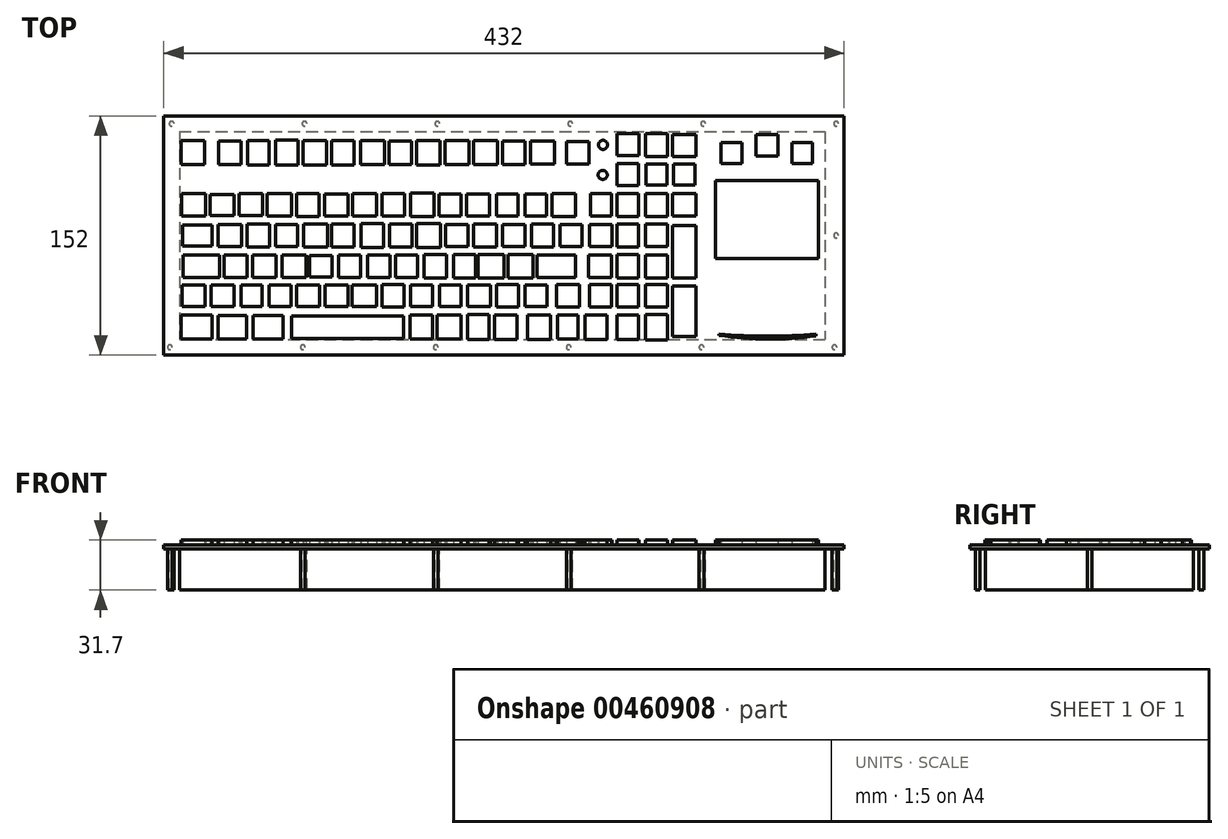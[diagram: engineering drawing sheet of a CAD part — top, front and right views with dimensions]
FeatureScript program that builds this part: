
annotation { "Feature Type Name" : "Feature", "Feature Type Description" : "" }
export const myFeature = defineFeature(function(context is Context, id is Id, definition is map)
    precondition{}
    {
        {
            var Q0;
            Q0=qCreatedBy(makeId("Top.planeOp"),FACE);
            var sketch = newSketch(context, id + "F0", { "sketchPlane" : qUnion([Q0])});
            skLineSegment(sketch, "E0.bottom", {"start": v(216, 76) * mm, "end": v(-216, 76) * mm});
            skLineSegment(sketch, "E0.top", {"start": v(216, -76) * mm, "end": v(-216, -76) * mm});
            skLineSegment(sketch, "E0.left", {"start": v(216, 76) * mm, "end": v(216, -76) * mm});
            skLineSegment(sketch, "E0.right", {"start": v(-216, 76) * mm, "end": v(-216, -76) * mm});
            skPoint(sketch, "E0.middle", {"position": v(0, 0) * mm});
            skLineSegment(sketch, "E1", {"start": v(-197.56, 52.6) * mm, "end": v(47, 52.6) * mm, "construction": true});
            skLineSegment(sketch, "E2", {"start": v(78.75, 57.78) * mm, "end": v(78.75, -58.22) * mm, "construction": true});
            skLineSegment(sketch, "E3", {"start": v(96.86, 57.48) * mm, "end": v(96.86, -58.22) * mm, "construction": true});
            skLineSegment(sketch, "E4", {"start": v(114.66, 58.09) * mm, "end": v(114.66, -58.22) * mm, "construction": true});
            skLineSegment(sketch, "E5", {"start": v(-195.3, -58.22) * mm, "end": v(114.66, -58.22) * mm, "construction": true});
            skLineSegment(sketch, "E6", {"start": v(-197.14, -38.27) * mm, "end": v(114.66, -38.27) * mm, "construction": true});
            skLineSegment(sketch, "E7", {"start": v(-196.22, -19.55) * mm, "end": v(114.66, -19.55) * mm, "construction": true});
            skLineSegment(sketch, "E8", {"start": v(-194.68, 0) * mm, "end": v(114.66, 0) * mm, "construction": true});
            skLineSegment(sketch, "E9", {"start": v(-197.14, 19.42) * mm, "end": v(114.66, 19.42) * mm, "construction": true});
            skLineSegment(sketch, "E10", {"start": v(134.3, -14.64) * mm, "end": v(199.67, 34.77) * mm, "construction": true});
            skLineSegment(sketch, "E11", {"start": v(137.98, 45.81) * mm, "end": v(151.36, 59.04) * mm, "construction": true});
            skLineSegment(sketch, "E12", {"start": v(160.21, 50.47) * mm, "end": v(174.17, 64.15) * mm, "construction": true});
            skLineSegment(sketch, "E13", {"start": v(183.02, 45.63) * mm, "end": v(196.16, 58.95) * mm, "construction": true});
            skLineSegment(sketch, "E14", {"start": v(78.75, 38.8) * mm, "end": v(114.66, 38.8) * mm, "construction": true});
            skLineSegment(sketch, "E15.bottom", {"start": v(199.67, 34.77) * mm, "end": v(134.3, 34.77) * mm});
            skLineSegment(sketch, "E15.top", {"start": v(199.67, -14.64) * mm, "end": v(134.3, -14.64) * mm});
            skLineSegment(sketch, "E15.left", {"start": v(199.67, 34.77) * mm, "end": v(199.67, -14.64) * mm});
            skLineSegment(sketch, "E15.right", {"start": v(134.3, 34.77) * mm, "end": v(134.3, -14.64) * mm});
            skPoint(sketch, "E15.middle", {"position": v(166.98, 10.06) * mm});
            skLineSegment(sketch, "E16.bottom", {"start": v(151.36, 59.04) * mm, "end": v(137.98, 59.04) * mm});
            skLineSegment(sketch, "E16.top", {"start": v(151.36, 45.81) * mm, "end": v(137.98, 45.81) * mm});
            skLineSegment(sketch, "E16.left", {"start": v(151.36, 59.04) * mm, "end": v(151.36, 45.81) * mm});
            skLineSegment(sketch, "E16.right", {"start": v(137.98, 59.04) * mm, "end": v(137.98, 45.81) * mm});
            skPoint(sketch, "E16.middle", {"position": v(144.67, 52.43) * mm});
            skLineSegment(sketch, "E17.bottom", {"start": v(174.17, 64.15) * mm, "end": v(160.21, 64.15) * mm});
            skLineSegment(sketch, "E17.top", {"start": v(174.17, 50.47) * mm, "end": v(160.21, 50.47) * mm});
            skLineSegment(sketch, "E17.left", {"start": v(174.17, 64.15) * mm, "end": v(174.17, 50.47) * mm});
            skLineSegment(sketch, "E17.right", {"start": v(160.21, 64.15) * mm, "end": v(160.21, 50.47) * mm});
            skPoint(sketch, "E17.middle", {"position": v(167.2, 57.31) * mm});
            skLineSegment(sketch, "E18.bottom", {"start": v(196.16, 58.95) * mm, "end": v(183.02, 58.95) * mm});
            skLineSegment(sketch, "E18.top", {"start": v(196.16, 45.63) * mm, "end": v(183.02, 45.63) * mm});
            skLineSegment(sketch, "E18.left", {"start": v(196.16, 58.95) * mm, "end": v(196.16, 45.63) * mm});
            skLineSegment(sketch, "E18.right", {"start": v(183.02, 58.95) * mm, "end": v(183.02, 45.63) * mm});
            skPoint(sketch, "E18.middle", {"position": v(189.59, 52.3) * mm});
            skLineSegment(sketch, "E19.bottom", {"start": v(122.07, 64.09) * mm, "end": v(107.24, 64.09) * mm});
            skLineSegment(sketch, "E19.top", {"start": v(122.07, 50.04) * mm, "end": v(107.24, 50.04) * mm});
            skLineSegment(sketch, "E19.left", {"start": v(122.07, 64.09) * mm, "end": v(122.07, 50.04) * mm});
            skLineSegment(sketch, "E19.right", {"start": v(107.24, 64.09) * mm, "end": v(107.24, 50.04) * mm});
            skPoint(sketch, "E19.middle", {"position": v(114.66, 57.06) * mm});
            skLineSegment(sketch, "E20.bottom", {"start": v(103.83, 64.73) * mm, "end": v(89.9, 64.73) * mm});
            skLineSegment(sketch, "E20.top", {"start": v(103.83, 50.22) * mm, "end": v(89.9, 50.22) * mm});
            skLineSegment(sketch, "E20.left", {"start": v(103.83, 64.73) * mm, "end": v(103.83, 50.22) * mm});
            skLineSegment(sketch, "E20.right", {"start": v(89.9, 64.73) * mm, "end": v(89.9, 50.22) * mm});
            skPoint(sketch, "E20.middle", {"position": v(96.86, 57.48) * mm});
            skLineSegment(sketch, "E21.bottom", {"start": v(85.76, 64.73) * mm, "end": v(71.75, 64.73) * mm});
            skLineSegment(sketch, "E21.top", {"start": v(85.76, 50.84) * mm, "end": v(71.75, 50.84) * mm});
            skLineSegment(sketch, "E21.left", {"start": v(85.76, 64.73) * mm, "end": v(85.76, 50.84) * mm});
            skLineSegment(sketch, "E21.right", {"start": v(71.75, 64.73) * mm, "end": v(71.75, 50.84) * mm});
            skPoint(sketch, "E21.middle", {"position": v(78.75, 57.78) * mm});
            skLineSegment(sketch, "E22.bottom", {"start": v(85.67, 45.75) * mm, "end": v(71.84, 45.75) * mm});
            skLineSegment(sketch, "E22.top", {"start": v(85.67, 31.84) * mm, "end": v(71.84, 31.84) * mm});
            skLineSegment(sketch, "E22.left", {"start": v(85.67, 45.75) * mm, "end": v(85.67, 31.84) * mm});
            skLineSegment(sketch, "E22.right", {"start": v(71.84, 45.75) * mm, "end": v(71.84, 31.84) * mm});
            skPoint(sketch, "E22.middle", {"position": v(78.75, 38.8) * mm});
            skLineSegment(sketch, "E23.bottom", {"start": v(103.55, 45.48) * mm, "end": v(90.17, 45.48) * mm});
            skLineSegment(sketch, "E23.top", {"start": v(103.55, 32.1) * mm, "end": v(90.17, 32.1) * mm});
            skLineSegment(sketch, "E23.left", {"start": v(103.55, 45.48) * mm, "end": v(103.55, 32.1) * mm});
            skLineSegment(sketch, "E23.right", {"start": v(90.17, 45.48) * mm, "end": v(90.17, 32.1) * mm});
            skPoint(sketch, "E23.middle", {"position": v(96.86, 38.8) * mm});
            skLineSegment(sketch, "E24.bottom", {"start": v(121.53, 45.39) * mm, "end": v(107.8, 45.39) * mm});
            skLineSegment(sketch, "E24.top", {"start": v(121.53, 32.2) * mm, "end": v(107.8, 32.2) * mm});
            skLineSegment(sketch, "E24.left", {"start": v(121.53, 45.39) * mm, "end": v(121.53, 32.2) * mm});
            skLineSegment(sketch, "E24.right", {"start": v(107.8, 45.39) * mm, "end": v(107.8, 32.2) * mm});
            skPoint(sketch, "E24.middle", {"position": v(114.66, 38.8) * mm});
            skLineSegment(sketch, "E25.bottom", {"start": v(122.07, 26.58) * mm, "end": v(107.24, 26.58) * mm});
            skLineSegment(sketch, "E25.top", {"start": v(122.07, 12.26) * mm, "end": v(107.24, 12.26) * mm});
            skLineSegment(sketch, "E25.left", {"start": v(122.07, 26.58) * mm, "end": v(122.07, 12.26) * mm});
            skLineSegment(sketch, "E25.right", {"start": v(107.24, 26.58) * mm, "end": v(107.24, 12.26) * mm});
            skPoint(sketch, "E25.middle", {"position": v(114.66, 19.42) * mm});
            skLineSegment(sketch, "E26.bottom", {"start": v(103.86, 26.67) * mm, "end": v(89.86, 26.67) * mm});
            skLineSegment(sketch, "E26.top", {"start": v(103.86, 12.17) * mm, "end": v(89.86, 12.17) * mm});
            skLineSegment(sketch, "E26.left", {"start": v(103.86, 26.67) * mm, "end": v(103.86, 12.17) * mm});
            skLineSegment(sketch, "E26.right", {"start": v(89.86, 26.67) * mm, "end": v(89.86, 12.17) * mm});
            skPoint(sketch, "E26.middle", {"position": v(96.86, 19.42) * mm});
            skLineSegment(sketch, "E27.bottom", {"start": v(85.61, 26.76) * mm, "end": v(71.9, 26.76) * mm});
            skLineSegment(sketch, "E27.top", {"start": v(85.61, 12.08) * mm, "end": v(71.9, 12.08) * mm});
            skLineSegment(sketch, "E27.left", {"start": v(85.61, 26.76) * mm, "end": v(85.61, 12.08) * mm});
            skLineSegment(sketch, "E27.right", {"start": v(71.9, 26.76) * mm, "end": v(71.9, 12.08) * mm});
            skPoint(sketch, "E27.middle", {"position": v(78.75, 19.42) * mm});
            skLineSegment(sketch, "E28.bottom", {"start": v(122.07, 6.26) * mm, "end": v(107.24, 6.26) * mm});
            skLineSegment(sketch, "E28.top", {"start": v(122.07, -27.15) * mm, "end": v(107.24, -27.15) * mm});
            skLineSegment(sketch, "E28.left", {"start": v(122.07, 6.26) * mm, "end": v(122.07, -27.15) * mm});
            skLineSegment(sketch, "E28.right", {"start": v(107.24, 6.26) * mm, "end": v(107.24, -27.15) * mm});
            skPoint(sketch, "E28.middle", {"position": v(114.66, -10.45) * mm});
            skLineSegment(sketch, "E29.bottom", {"start": v(122.07, -31.95) * mm, "end": v(107.24, -31.95) * mm});
            skLineSegment(sketch, "E29.top", {"start": v(122.07, -64.28) * mm, "end": v(107.24, -64.28) * mm});
            skLineSegment(sketch, "E29.left", {"start": v(122.07, -31.95) * mm, "end": v(122.07, -64.28) * mm});
            skLineSegment(sketch, "E29.right", {"start": v(107.24, -31.95) * mm, "end": v(107.24, -64.28) * mm});
            skPoint(sketch, "E29.middle", {"position": v(114.66, -48.11) * mm});
            skLineSegment(sketch, "E30.bottom", {"start": v(103.79, 7.16) * mm, "end": v(89.93, 7.16) * mm});
            skLineSegment(sketch, "E30.top", {"start": v(103.79, -7.16) * mm, "end": v(89.93, -7.16) * mm});
            skLineSegment(sketch, "E30.left", {"start": v(103.79, 7.16) * mm, "end": v(103.79, -7.16) * mm});
            skLineSegment(sketch, "E30.right", {"start": v(89.93, 7.16) * mm, "end": v(89.93, -7.16) * mm});
            skPoint(sketch, "E30.middle", {"position": v(96.86, 0) * mm});
            skLineSegment(sketch, "E31.bottom", {"start": v(85.61, 7.39) * mm, "end": v(71.9, 7.39) * mm});
            skLineSegment(sketch, "E31.top", {"start": v(85.61, -7.39) * mm, "end": v(71.9, -7.39) * mm});
            skLineSegment(sketch, "E31.left", {"start": v(85.61, 7.39) * mm, "end": v(85.61, -7.39) * mm});
            skLineSegment(sketch, "E31.right", {"start": v(71.9, 7.39) * mm, "end": v(71.9, -7.39) * mm});
            skPoint(sketch, "E31.middle", {"position": v(78.75, 0) * mm});
            skLineSegment(sketch, "E32.bottom", {"start": v(85.61, -12.18) * mm, "end": v(71.9, -12.18) * mm});
            skLineSegment(sketch, "E32.top", {"start": v(85.61, -26.93) * mm, "end": v(71.9, -26.93) * mm});
            skLineSegment(sketch, "E32.left", {"start": v(85.61, -12.18) * mm, "end": v(85.61, -26.93) * mm});
            skLineSegment(sketch, "E32.right", {"start": v(71.9, -12.18) * mm, "end": v(71.9, -26.93) * mm});
            skPoint(sketch, "E32.middle", {"position": v(78.75, -19.55) * mm});
            skLineSegment(sketch, "E33.bottom", {"start": v(103.86, -12.25) * mm, "end": v(89.86, -12.25) * mm});
            skLineSegment(sketch, "E33.top", {"start": v(103.86, -26.85) * mm, "end": v(89.86, -26.85) * mm});
            skLineSegment(sketch, "E33.left", {"start": v(103.86, -12.25) * mm, "end": v(103.86, -26.85) * mm});
            skLineSegment(sketch, "E33.right", {"start": v(89.86, -12.25) * mm, "end": v(89.86, -26.85) * mm});
            skPoint(sketch, "E33.middle", {"position": v(96.86, -19.55) * mm});
            skLineSegment(sketch, "E34.bottom", {"start": v(85.61, -31.27) * mm, "end": v(71.9, -31.27) * mm});
            skLineSegment(sketch, "E34.top", {"start": v(85.61, -45.28) * mm, "end": v(71.9, -45.28) * mm});
            skLineSegment(sketch, "E34.left", {"start": v(85.61, -31.27) * mm, "end": v(85.61, -45.28) * mm});
            skLineSegment(sketch, "E34.right", {"start": v(71.9, -31.27) * mm, "end": v(71.9, -45.28) * mm});
            skPoint(sketch, "E34.middle", {"position": v(78.75, -38.27) * mm});
            skLineSegment(sketch, "E35.bottom", {"start": v(103.86, -31.18) * mm, "end": v(89.86, -31.18) * mm});
            skLineSegment(sketch, "E35.top", {"start": v(103.86, -45.37) * mm, "end": v(89.86, -45.37) * mm});
            skLineSegment(sketch, "E35.left", {"start": v(103.86, -31.18) * mm, "end": v(103.86, -45.37) * mm});
            skLineSegment(sketch, "E35.right", {"start": v(89.86, -31.18) * mm, "end": v(89.86, -45.37) * mm});
            skPoint(sketch, "E35.middle", {"position": v(96.86, -38.27) * mm});
            skLineSegment(sketch, "E36.bottom", {"start": v(85.61, -50.52) * mm, "end": v(71.9, -50.52) * mm});
            skLineSegment(sketch, "E36.top", {"start": v(85.61, -65.92) * mm, "end": v(71.9, -65.92) * mm});
            skLineSegment(sketch, "E36.left", {"start": v(85.61, -50.52) * mm, "end": v(85.61, -65.92) * mm});
            skLineSegment(sketch, "E36.right", {"start": v(71.9, -50.52) * mm, "end": v(71.9, -65.92) * mm});
            skPoint(sketch, "E36.middle", {"position": v(78.75, -58.22) * mm});
            skLineSegment(sketch, "E37.bottom", {"start": v(103.86, -50.15) * mm, "end": v(89.86, -50.15) * mm});
            skLineSegment(sketch, "E37.top", {"start": v(103.86, -66.28) * mm, "end": v(89.86, -66.28) * mm});
            skLineSegment(sketch, "E37.left", {"start": v(103.86, -50.15) * mm, "end": v(103.86, -66.28) * mm});
            skLineSegment(sketch, "E37.right", {"start": v(89.86, -50.15) * mm, "end": v(89.86, -66.28) * mm});
            skPoint(sketch, "E37.middle", {"position": v(96.86, -58.22) * mm});
            skLineSegment(sketch, "E38.bottom", {"start": v(65.58, -50.52) * mm, "end": v(51.47, -50.52) * mm});
            skLineSegment(sketch, "E38.top", {"start": v(65.58, -65.92) * mm, "end": v(51.47, -65.92) * mm});
            skLineSegment(sketch, "E38.left", {"start": v(65.58, -50.52) * mm, "end": v(65.58, -65.92) * mm});
            skLineSegment(sketch, "E38.right", {"start": v(51.47, -50.52) * mm, "end": v(51.47, -65.92) * mm});
            skPoint(sketch, "E38.middle", {"position": v(58.53, -58.22) * mm});
            skPoint(sketch, "E38.cornerSnap0", {"position": v(78.75, -50.52) * mm});
            skLineSegment(sketch, "E39.bottom", {"start": v(47.24, -50.62) * mm, "end": v(34, -50.62) * mm});
            skLineSegment(sketch, "E39.top", {"start": v(47.24, -65.82) * mm, "end": v(34, -65.82) * mm});
            skLineSegment(sketch, "E39.left", {"start": v(47.24, -50.62) * mm, "end": v(47.24, -65.82) * mm});
            skLineSegment(sketch, "E39.right", {"start": v(34, -50.62) * mm, "end": v(34, -65.82) * mm});
            skPoint(sketch, "E39.middle", {"position": v(40.62, -58.22) * mm});
            skLineSegment(sketch, "E40.bottom", {"start": v(29.56, -50.4) * mm, "end": v(15.02, -50.4) * mm});
            skLineSegment(sketch, "E40.top", {"start": v(29.56, -66.04) * mm, "end": v(15.02, -66.04) * mm});
            skLineSegment(sketch, "E40.left", {"start": v(29.56, -50.4) * mm, "end": v(29.56, -66.04) * mm});
            skLineSegment(sketch, "E40.right", {"start": v(15.02, -50.4) * mm, "end": v(15.02, -66.04) * mm});
            skPoint(sketch, "E40.middle", {"position": v(22.29, -58.22) * mm});
            skLineSegment(sketch, "E41.bottom", {"start": v(8.4, -50.4) * mm, "end": v(-5.92, -50.4) * mm});
            skLineSegment(sketch, "E41.top", {"start": v(8.4, -66.04) * mm, "end": v(-5.92, -66.04) * mm});
            skLineSegment(sketch, "E41.left", {"start": v(8.4, -50.4) * mm, "end": v(8.4, -66.04) * mm});
            skLineSegment(sketch, "E41.right", {"start": v(-5.92, -50.4) * mm, "end": v(-5.92, -66.04) * mm});
            skPoint(sketch, "E41.middle", {"position": v(1.24, -58.22) * mm});
            skLineSegment(sketch, "E42.bottom", {"start": v(-9.28, -50.28) * mm, "end": v(-22.96, -50.28) * mm});
            skLineSegment(sketch, "E42.top", {"start": v(-9.28, -66.16) * mm, "end": v(-22.96, -66.16) * mm});
            skLineSegment(sketch, "E42.left", {"start": v(-9.28, -50.28) * mm, "end": v(-9.28, -66.16) * mm});
            skLineSegment(sketch, "E42.right", {"start": v(-22.96, -50.28) * mm, "end": v(-22.96, -66.16) * mm});
            skPoint(sketch, "E42.middle", {"position": v(-16.12, -58.22) * mm});
            skLineSegment(sketch, "E43.bottom", {"start": v(-27.34, -50.56) * mm, "end": v(-42.3, -50.56) * mm});
            skLineSegment(sketch, "E43.top", {"start": v(-27.34, -65.88) * mm, "end": v(-42.3, -65.88) * mm});
            skLineSegment(sketch, "E43.left", {"start": v(-27.34, -50.56) * mm, "end": v(-27.34, -65.88) * mm});
            skLineSegment(sketch, "E43.right", {"start": v(-42.3, -50.56) * mm, "end": v(-42.3, -65.88) * mm});
            skPoint(sketch, "E43.middle", {"position": v(-34.82, -58.22) * mm});
            skLineSegment(sketch, "E44.bottom", {"start": v(-45.4, -50.65) * mm, "end": v(-59.64, -50.65) * mm});
            skLineSegment(sketch, "E44.top", {"start": v(-45.4, -65.8) * mm, "end": v(-59.64, -65.8) * mm});
            skLineSegment(sketch, "E44.left", {"start": v(-45.4, -50.65) * mm, "end": v(-45.4, -65.8) * mm});
            skLineSegment(sketch, "E44.right", {"start": v(-59.64, -50.65) * mm, "end": v(-59.64, -65.8) * mm});
            skPoint(sketch, "E44.middle", {"position": v(-52.52, -58.22) * mm});
            skLineSegment(sketch, "E45.bottom", {"start": v(-63.58, -51.12) * mm, "end": v(-134.75, -51.12) * mm});
            skLineSegment(sketch, "E45.top", {"start": v(-63.58, -65.32) * mm, "end": v(-134.75, -65.32) * mm});
            skLineSegment(sketch, "E45.left", {"start": v(-63.58, -51.12) * mm, "end": v(-63.58, -65.32) * mm});
            skLineSegment(sketch, "E45.right", {"start": v(-134.75, -51.12) * mm, "end": v(-134.75, -65.32) * mm});
            skPoint(sketch, "E45.middle", {"position": v(-99.17, -58.22) * mm});
            skLineSegment(sketch, "E46.bottom", {"start": v(-140.19, -50.78) * mm, "end": v(-159.28, -50.78) * mm});
            skLineSegment(sketch, "E46.top", {"start": v(-140.19, -65.66) * mm, "end": v(-159.28, -65.66) * mm});
            skLineSegment(sketch, "E46.left", {"start": v(-140.19, -50.78) * mm, "end": v(-140.19, -65.66) * mm});
            skLineSegment(sketch, "E46.right", {"start": v(-159.28, -50.78) * mm, "end": v(-159.28, -65.66) * mm});
            skPoint(sketch, "E46.middle", {"position": v(-149.73, -58.22) * mm});
            skLineSegment(sketch, "E47.bottom", {"start": v(-163.28, -50.78) * mm, "end": v(-181.35, -50.78) * mm});
            skLineSegment(sketch, "E47.top", {"start": v(-163.28, -65.66) * mm, "end": v(-181.35, -65.66) * mm});
            skLineSegment(sketch, "E47.left", {"start": v(-163.28, -50.78) * mm, "end": v(-163.28, -65.66) * mm});
            skLineSegment(sketch, "E47.right", {"start": v(-181.35, -50.78) * mm, "end": v(-181.35, -65.66) * mm});
            skPoint(sketch, "E47.middle", {"position": v(-172.32, -58.22) * mm});
            skLineSegment(sketch, "E48.bottom", {"start": v(-185.45, -50.55) * mm, "end": v(-205.14, -50.55) * mm});
            skLineSegment(sketch, "E48.top", {"start": v(-185.45, -65.9) * mm, "end": v(-205.14, -65.9) * mm});
            skLineSegment(sketch, "E48.left", {"start": v(-185.45, -50.55) * mm, "end": v(-185.45, -65.9) * mm});
            skLineSegment(sketch, "E48.right", {"start": v(-205.14, -50.55) * mm, "end": v(-205.14, -65.9) * mm});
            skPoint(sketch, "E48.middle", {"position": v(-195.3, -58.22) * mm});
            skLineSegment(sketch, "E49.bottom", {"start": v(-189.83, -31.56) * mm, "end": v(-204.44, -31.56) * mm});
            skLineSegment(sketch, "E49.top", {"start": v(-189.83, -44.98) * mm, "end": v(-204.44, -44.98) * mm});
            skLineSegment(sketch, "E49.left", {"start": v(-189.83, -31.56) * mm, "end": v(-189.83, -44.98) * mm});
            skLineSegment(sketch, "E49.right", {"start": v(-204.44, -31.56) * mm, "end": v(-204.44, -44.98) * mm});
            skPoint(sketch, "E49.middle", {"position": v(-197.14, -38.27) * mm});
            skLineSegment(sketch, "E50.bottom", {"start": v(-171.39, -31.35) * mm, "end": v(-185.93, -31.35) * mm});
            skLineSegment(sketch, "E50.top", {"start": v(-171.39, -45.2) * mm, "end": v(-185.93, -45.2) * mm});
            skLineSegment(sketch, "E50.left", {"start": v(-171.39, -31.35) * mm, "end": v(-171.39, -45.2) * mm});
            skLineSegment(sketch, "E50.right", {"start": v(-185.93, -31.35) * mm, "end": v(-185.93, -45.2) * mm});
            skPoint(sketch, "E50.middle", {"position": v(-178.66, -38.27) * mm});
            skLineSegment(sketch, "E51.bottom", {"start": v(-153.48, -31.46) * mm, "end": v(-166.94, -31.46) * mm});
            skLineSegment(sketch, "E51.top", {"start": v(-153.48, -45.09) * mm, "end": v(-166.94, -45.09) * mm});
            skLineSegment(sketch, "E51.left", {"start": v(-153.48, -31.46) * mm, "end": v(-153.48, -45.09) * mm});
            skLineSegment(sketch, "E51.right", {"start": v(-166.94, -31.46) * mm, "end": v(-166.94, -45.09) * mm});
            skPoint(sketch, "E51.middle", {"position": v(-160.21, -38.27) * mm});
            skLineSegment(sketch, "E52.bottom", {"start": v(-135.26, -31.46) * mm, "end": v(-149.14, -31.46) * mm});
            skLineSegment(sketch, "E52.top", {"start": v(-135.26, -45.09) * mm, "end": v(-149.14, -45.09) * mm});
            skLineSegment(sketch, "E52.left", {"start": v(-135.26, -31.46) * mm, "end": v(-135.26, -45.09) * mm});
            skLineSegment(sketch, "E52.right", {"start": v(-149.14, -31.46) * mm, "end": v(-149.14, -45.09) * mm});
            skPoint(sketch, "E52.middle", {"position": v(-142.2, -38.27) * mm});
            skLineSegment(sketch, "E53.bottom", {"start": v(-117.03, -31.46) * mm, "end": v(-131.57, -31.46) * mm});
            skLineSegment(sketch, "E53.top", {"start": v(-117.03, -45.09) * mm, "end": v(-131.57, -45.09) * mm});
            skLineSegment(sketch, "E53.left", {"start": v(-117.03, -31.46) * mm, "end": v(-117.03, -45.09) * mm});
            skLineSegment(sketch, "E53.right", {"start": v(-131.57, -31.46) * mm, "end": v(-131.57, -45.09) * mm});
            skPoint(sketch, "E53.middle", {"position": v(-124.3, -38.27) * mm});
            skLineSegment(sketch, "E54.bottom", {"start": v(-98.9, -31.35) * mm, "end": v(-113.67, -31.35) * mm});
            skLineSegment(sketch, "E54.top", {"start": v(-98.9, -45.2) * mm, "end": v(-113.67, -45.2) * mm});
            skLineSegment(sketch, "E54.left", {"start": v(-98.9, -31.35) * mm, "end": v(-98.9, -45.2) * mm});
            skLineSegment(sketch, "E54.right", {"start": v(-113.67, -31.35) * mm, "end": v(-113.67, -45.2) * mm});
            skPoint(sketch, "E54.middle", {"position": v(-106.29, -38.27) * mm});
            skLineSegment(sketch, "E55.bottom", {"start": v(-80.86, -31.36) * mm, "end": v(-96.51, -31.36) * mm});
            skLineSegment(sketch, "E55.top", {"start": v(-80.86, -45.19) * mm, "end": v(-96.51, -45.19) * mm});
            skLineSegment(sketch, "E55.left", {"start": v(-80.86, -31.36) * mm, "end": v(-80.86, -45.19) * mm});
            skLineSegment(sketch, "E55.right", {"start": v(-96.51, -31.36) * mm, "end": v(-96.51, -45.19) * mm});
            skPoint(sketch, "E55.middle", {"position": v(-88.69, -38.27) * mm});
            skLineSegment(sketch, "E56.bottom", {"start": v(-63.52, -31.05) * mm, "end": v(-77.33, -31.05) * mm});
            skLineSegment(sketch, "E56.top", {"start": v(-63.52, -45.5) * mm, "end": v(-77.33, -45.5) * mm});
            skLineSegment(sketch, "E56.left", {"start": v(-63.52, -31.05) * mm, "end": v(-63.52, -45.5) * mm});
            skLineSegment(sketch, "E56.right", {"start": v(-77.33, -31.05) * mm, "end": v(-77.33, -45.5) * mm});
            skPoint(sketch, "E56.middle", {"position": v(-70.43, -38.27) * mm});
            skLineSegment(sketch, "E57.bottom", {"start": v(-45.4, -31.36) * mm, "end": v(-59.24, -31.36) * mm});
            skLineSegment(sketch, "E57.top", {"start": v(-45.4, -45.19) * mm, "end": v(-59.24, -45.19) * mm});
            skLineSegment(sketch, "E57.left", {"start": v(-45.4, -31.36) * mm, "end": v(-45.4, -45.19) * mm});
            skLineSegment(sketch, "E57.right", {"start": v(-59.24, -31.36) * mm, "end": v(-59.24, -45.19) * mm});
            skPoint(sketch, "E57.middle", {"position": v(-52.32, -38.27) * mm});
            skLineSegment(sketch, "E58.bottom", {"start": v(-27.31, -31.51) * mm, "end": v(-40.81, -31.51) * mm});
            skLineSegment(sketch, "E58.top", {"start": v(-27.31, -45.03) * mm, "end": v(-40.81, -45.03) * mm});
            skLineSegment(sketch, "E58.left", {"start": v(-27.31, -31.51) * mm, "end": v(-27.31, -45.03) * mm});
            skLineSegment(sketch, "E58.right", {"start": v(-40.81, -31.51) * mm, "end": v(-40.81, -45.03) * mm});
            skPoint(sketch, "E58.middle", {"position": v(-34.06, -38.27) * mm});
            skLineSegment(sketch, "E59.bottom", {"start": v(-8.6, -31.36) * mm, "end": v(-23.01, -31.36) * mm});
            skLineSegment(sketch, "E59.top", {"start": v(-8.6, -45.19) * mm, "end": v(-23.01, -45.19) * mm});
            skLineSegment(sketch, "E59.left", {"start": v(-8.6, -31.36) * mm, "end": v(-8.6, -45.19) * mm});
            skLineSegment(sketch, "E59.right", {"start": v(-23.01, -31.36) * mm, "end": v(-23.01, -45.19) * mm});
            skPoint(sketch, "E59.middle", {"position": v(-15.8, -38.27) * mm});
            skLineSegment(sketch, "E60.bottom", {"start": v(9.2, -31.2) * mm, "end": v(-4.6, -31.2) * mm});
            skLineSegment(sketch, "E60.top", {"start": v(9.2, -45.34) * mm, "end": v(-4.6, -45.34) * mm});
            skLineSegment(sketch, "E60.left", {"start": v(9.2, -31.2) * mm, "end": v(9.2, -45.34) * mm});
            skLineSegment(sketch, "E60.right", {"start": v(-4.6, -31.2) * mm, "end": v(-4.6, -45.34) * mm});
            skPoint(sketch, "E60.middle", {"position": v(2.3, -38.27) * mm});
            skLineSegment(sketch, "E61.bottom", {"start": v(27.47, -31.36) * mm, "end": v(13.35, -31.36) * mm});
            skLineSegment(sketch, "E61.top", {"start": v(27.47, -45.19) * mm, "end": v(13.35, -45.19) * mm});
            skLineSegment(sketch, "E61.left", {"start": v(27.47, -31.36) * mm, "end": v(27.47, -45.19) * mm});
            skLineSegment(sketch, "E61.right", {"start": v(13.35, -31.36) * mm, "end": v(13.35, -45.19) * mm});
            skPoint(sketch, "E61.middle", {"position": v(20.4, -38.27) * mm});
            skLineSegment(sketch, "E62.bottom", {"start": v(48.18, -31.2) * mm, "end": v(33.45, -31.2) * mm});
            skLineSegment(sketch, "E62.top", {"start": v(48.18, -45.34) * mm, "end": v(33.45, -45.34) * mm});
            skLineSegment(sketch, "E62.left", {"start": v(48.18, -31.2) * mm, "end": v(48.18, -45.34) * mm});
            skLineSegment(sketch, "E62.right", {"start": v(33.45, -31.2) * mm, "end": v(33.45, -45.34) * mm});
            skPoint(sketch, "E62.middle", {"position": v(40.82, -38.27) * mm});
            skLineSegment(sketch, "E63.bottom", {"start": v(68.28, -31.2) * mm, "end": v(54.47, -31.2) * mm});
            skLineSegment(sketch, "E63.top", {"start": v(68.28, -45.34) * mm, "end": v(54.47, -45.34) * mm});
            skLineSegment(sketch, "E63.left", {"start": v(68.28, -31.2) * mm, "end": v(68.28, -45.34) * mm});
            skLineSegment(sketch, "E63.right", {"start": v(54.47, -31.2) * mm, "end": v(54.47, -45.34) * mm});
            skPoint(sketch, "E63.middle", {"position": v(61.38, -38.27) * mm});
            skLineSegment(sketch, "E64.bottom", {"start": v(68.28, -12.33) * mm, "end": v(53.86, -12.33) * mm});
            skLineSegment(sketch, "E64.top", {"start": v(68.28, -26.77) * mm, "end": v(53.86, -26.77) * mm});
            skLineSegment(sketch, "E64.left", {"start": v(68.28, -12.33) * mm, "end": v(68.28, -26.77) * mm});
            skLineSegment(sketch, "E64.right", {"start": v(53.86, -12.33) * mm, "end": v(53.86, -26.77) * mm});
            skPoint(sketch, "E64.middle", {"position": v(61.07, -19.55) * mm});
            skLineSegment(sketch, "E65.bottom", {"start": v(45.42, -12.48) * mm, "end": v(21.18, -12.48) * mm});
            skLineSegment(sketch, "E65.top", {"start": v(45.42, -26.62) * mm, "end": v(21.18, -26.62) * mm});
            skLineSegment(sketch, "E65.left", {"start": v(45.42, -12.48) * mm, "end": v(45.42, -26.62) * mm});
            skLineSegment(sketch, "E65.right", {"start": v(21.18, -12.48) * mm, "end": v(21.18, -26.62) * mm});
            skPoint(sketch, "E65.middle", {"position": v(33.3, -19.55) * mm});
            skLineSegment(sketch, "E66.bottom", {"start": v(18.42, -12.02) * mm, "end": v(2.76, -12.02) * mm});
            skLineSegment(sketch, "E66.top", {"start": v(18.42, -27.08) * mm, "end": v(2.76, -27.08) * mm});
            skLineSegment(sketch, "E66.left", {"start": v(18.42, -12.02) * mm, "end": v(18.42, -27.08) * mm});
            skLineSegment(sketch, "E66.right", {"start": v(2.76, -12.02) * mm, "end": v(2.76, -27.08) * mm});
            skPoint(sketch, "E66.middle", {"position": v(10.59, -19.55) * mm});
            skLineSegment(sketch, "E67.bottom", {"start": v(0, -12.02) * mm, "end": v(-16.26, -12.02) * mm});
            skLineSegment(sketch, "E67.top", {"start": v(0, -27.08) * mm, "end": v(-16.26, -27.08) * mm});
            skLineSegment(sketch, "E67.left", {"start": v(0, -12.02) * mm, "end": v(0, -27.08) * mm});
            skLineSegment(sketch, "E67.right", {"start": v(-16.26, -12.02) * mm, "end": v(-16.26, -27.08) * mm});
            skPoint(sketch, "E67.middle", {"position": v(-8.13, -19.55) * mm});
            skLineSegment(sketch, "E68.bottom", {"start": v(-17.93, -12.08) * mm, "end": v(-32, -12.08) * mm});
            skLineSegment(sketch, "E68.top", {"start": v(-17.93, -27.02) * mm, "end": v(-32, -27.02) * mm});
            skLineSegment(sketch, "E68.left", {"start": v(-17.93, -12.08) * mm, "end": v(-17.93, -27.02) * mm});
            skLineSegment(sketch, "E68.right", {"start": v(-32, -12.08) * mm, "end": v(-32, -27.02) * mm});
            skPoint(sketch, "E68.middle", {"position": v(-24.96, -19.55) * mm});
            skLineSegment(sketch, "E69.bottom", {"start": v(-36.5, -12.08) * mm, "end": v(-50.7, -12.08) * mm});
            skLineSegment(sketch, "E69.top", {"start": v(-36.5, -27.02) * mm, "end": v(-50.7, -27.02) * mm});
            skLineSegment(sketch, "E69.left", {"start": v(-36.5, -12.08) * mm, "end": v(-36.5, -27.02) * mm});
            skLineSegment(sketch, "E69.right", {"start": v(-50.7, -12.08) * mm, "end": v(-50.7, -27.02) * mm});
            skPoint(sketch, "E69.middle", {"position": v(-43.6, -19.55) * mm});
            skLineSegment(sketch, "E70.bottom", {"start": v(-54.96, -12.27) * mm, "end": v(-68.64, -12.27) * mm});
            skLineSegment(sketch, "E70.top", {"start": v(-54.96, -26.83) * mm, "end": v(-68.64, -26.83) * mm});
            skLineSegment(sketch, "E70.left", {"start": v(-54.96, -12.27) * mm, "end": v(-54.96, -26.83) * mm});
            skLineSegment(sketch, "E70.right", {"start": v(-68.64, -12.27) * mm, "end": v(-68.64, -26.83) * mm});
            skPoint(sketch, "E70.middle", {"position": v(-61.8, -19.55) * mm});
            skLineSegment(sketch, "E71.bottom", {"start": v(-72.44, -12.47) * mm, "end": v(-86.5, -12.47) * mm});
            skLineSegment(sketch, "E71.top", {"start": v(-72.44, -26.64) * mm, "end": v(-86.5, -26.64) * mm});
            skLineSegment(sketch, "E71.left", {"start": v(-72.44, -12.47) * mm, "end": v(-72.44, -26.64) * mm});
            skLineSegment(sketch, "E71.right", {"start": v(-86.5, -12.47) * mm, "end": v(-86.5, -26.64) * mm});
            skPoint(sketch, "E71.middle", {"position": v(-79.47, -19.55) * mm});
            skLineSegment(sketch, "E72.bottom", {"start": v(-90.9, -12.52) * mm, "end": v(-104.87, -12.52) * mm});
            skLineSegment(sketch, "E72.top", {"start": v(-90.9, -26.58) * mm, "end": v(-104.87, -26.58) * mm});
            skLineSegment(sketch, "E72.left", {"start": v(-90.9, -12.52) * mm, "end": v(-90.9, -26.58) * mm});
            skLineSegment(sketch, "E72.right", {"start": v(-104.87, -12.52) * mm, "end": v(-104.87, -26.58) * mm});
            skPoint(sketch, "E72.middle", {"position": v(-97.89, -19.55) * mm});
            skLineSegment(sketch, "E73.bottom", {"start": v(-109.16, -12.6) * mm, "end": v(-123.43, -12.6) * mm});
            skLineSegment(sketch, "E73.top", {"start": v(-109.16, -26.5) * mm, "end": v(-123.43, -26.5) * mm});
            skLineSegment(sketch, "E73.left", {"start": v(-109.16, -12.6) * mm, "end": v(-109.16, -26.5) * mm});
            skLineSegment(sketch, "E73.right", {"start": v(-123.43, -12.6) * mm, "end": v(-123.43, -26.5) * mm});
            skPoint(sketch, "E73.middle", {"position": v(-116.3, -19.55) * mm});
            skLineSegment(sketch, "E74.bottom", {"start": v(-125.65, -12.42) * mm, "end": v(-140.84, -12.42) * mm});
            skLineSegment(sketch, "E74.top", {"start": v(-125.65, -26.69) * mm, "end": v(-140.84, -26.69) * mm});
            skLineSegment(sketch, "E74.left", {"start": v(-125.65, -12.42) * mm, "end": v(-125.65, -26.69) * mm});
            skLineSegment(sketch, "E74.right", {"start": v(-140.84, -12.42) * mm, "end": v(-140.84, -26.69) * mm});
            skPoint(sketch, "E74.middle", {"position": v(-133.25, -19.55) * mm});
            skLineSegment(sketch, "E75.bottom", {"start": v(-144.83, -12.34) * mm, "end": v(-159.56, -12.34) * mm});
            skLineSegment(sketch, "E75.top", {"start": v(-144.83, -26.76) * mm, "end": v(-159.56, -26.76) * mm});
            skLineSegment(sketch, "E75.left", {"start": v(-144.83, -12.34) * mm, "end": v(-144.83, -26.76) * mm});
            skLineSegment(sketch, "E75.right", {"start": v(-159.56, -12.34) * mm, "end": v(-159.56, -26.76) * mm});
            skPoint(sketch, "E75.middle", {"position": v(-152.2, -19.55) * mm});
            skLineSegment(sketch, "E76.bottom", {"start": v(-162.97, -12.28) * mm, "end": v(-177.56, -12.28) * mm});
            skLineSegment(sketch, "E76.top", {"start": v(-162.97, -26.82) * mm, "end": v(-177.56, -26.82) * mm});
            skLineSegment(sketch, "E76.left", {"start": v(-162.97, -12.28) * mm, "end": v(-162.97, -26.82) * mm});
            skLineSegment(sketch, "E76.right", {"start": v(-177.56, -12.28) * mm, "end": v(-177.56, -26.82) * mm});
            skPoint(sketch, "E76.middle", {"position": v(-170.26, -19.55) * mm});
            skLineSegment(sketch, "E77.bottom", {"start": v(-180.67, -12.56) * mm, "end": v(-203.66, -12.56) * mm});
            skLineSegment(sketch, "E77.top", {"start": v(-180.67, -26.55) * mm, "end": v(-203.66, -26.55) * mm});
            skLineSegment(sketch, "E77.left", {"start": v(-180.67, -12.56) * mm, "end": v(-180.67, -26.55) * mm});
            skLineSegment(sketch, "E77.right", {"start": v(-203.66, -12.56) * mm, "end": v(-203.66, -26.55) * mm});
            skPoint(sketch, "E77.middle", {"position": v(-192.16, -19.55) * mm});
            skLineSegment(sketch, "E78.bottom", {"start": v(-185.35, 6.74) * mm, "end": v(-204.01, 6.74) * mm});
            skLineSegment(sketch, "E78.top", {"start": v(-185.35, -6.74) * mm, "end": v(-204.01, -6.74) * mm});
            skLineSegment(sketch, "E78.left", {"start": v(-185.35, 6.74) * mm, "end": v(-185.35, -6.74) * mm});
            skLineSegment(sketch, "E78.right", {"start": v(-204.01, 6.74) * mm, "end": v(-204.01, -6.74) * mm});
            skPoint(sketch, "E78.middle", {"position": v(-194.68, 0) * mm});
            skLineSegment(sketch, "E79.bottom", {"start": v(-166.55, 7.05) * mm, "end": v(-181.43, 7.05) * mm});
            skLineSegment(sketch, "E79.top", {"start": v(-166.55, -7.05) * mm, "end": v(-181.43, -7.05) * mm});
            skLineSegment(sketch, "E79.left", {"start": v(-166.55, 7.05) * mm, "end": v(-166.55, -7.05) * mm});
            skLineSegment(sketch, "E79.right", {"start": v(-181.43, 7.05) * mm, "end": v(-181.43, -7.05) * mm});
            skPoint(sketch, "E79.middle", {"position": v(-174, 0) * mm});
            skLineSegment(sketch, "E80.bottom", {"start": v(-148.83, 7.28) * mm, "end": v(-162.94, 7.28) * mm});
            skLineSegment(sketch, "E80.top", {"start": v(-148.83, -7.28) * mm, "end": v(-162.94, -7.28) * mm});
            skLineSegment(sketch, "E80.left", {"start": v(-148.83, 7.28) * mm, "end": v(-148.83, -7.28) * mm});
            skLineSegment(sketch, "E80.right", {"start": v(-162.94, 7.28) * mm, "end": v(-162.94, -7.28) * mm});
            skPoint(sketch, "E80.middle", {"position": v(-155.89, 0) * mm});
            skLineSegment(sketch, "E81.bottom", {"start": v(-130.88, 7.05) * mm, "end": v(-145.15, 7.05) * mm});
            skLineSegment(sketch, "E81.top", {"start": v(-130.88, -7.05) * mm, "end": v(-145.15, -7.05) * mm});
            skLineSegment(sketch, "E81.left", {"start": v(-130.88, 7.05) * mm, "end": v(-130.88, -7.05) * mm});
            skLineSegment(sketch, "E81.right", {"start": v(-145.15, 7.05) * mm, "end": v(-145.15, -7.05) * mm});
            skPoint(sketch, "E81.middle", {"position": v(-138.01, 0) * mm});
            skLineSegment(sketch, "E82.bottom", {"start": v(-112, 7.2) * mm, "end": v(-127.04, 7.2) * mm});
            skLineSegment(sketch, "E82.top", {"start": v(-112, -7.2) * mm, "end": v(-127.04, -7.2) * mm});
            skLineSegment(sketch, "E82.left", {"start": v(-112, 7.2) * mm, "end": v(-112, -7.2) * mm});
            skLineSegment(sketch, "E82.right", {"start": v(-127.04, 7.2) * mm, "end": v(-127.04, -7.2) * mm});
            skPoint(sketch, "E82.middle", {"position": v(-119.52, 0) * mm});
            skLineSegment(sketch, "E83.bottom", {"start": v(-95.12, 7.37) * mm, "end": v(-109.35, 7.37) * mm});
            skLineSegment(sketch, "E83.top", {"start": v(-95.12, -7.37) * mm, "end": v(-109.35, -7.37) * mm});
            skLineSegment(sketch, "E83.left", {"start": v(-95.12, 7.37) * mm, "end": v(-95.12, -7.37) * mm});
            skLineSegment(sketch, "E83.right", {"start": v(-109.35, 7.37) * mm, "end": v(-109.35, -7.37) * mm});
            skPoint(sketch, "E83.middle", {"position": v(-102.23, 0) * mm});
            skLineSegment(sketch, "E84.bottom", {"start": v(-76.5, 7.56) * mm, "end": v(-90.74, 7.56) * mm});
            skLineSegment(sketch, "E84.top", {"start": v(-76.5, -7.56) * mm, "end": v(-90.74, -7.56) * mm});
            skLineSegment(sketch, "E84.left", {"start": v(-76.5, 7.56) * mm, "end": v(-76.5, -7.56) * mm});
            skLineSegment(sketch, "E84.right", {"start": v(-90.74, 7.56) * mm, "end": v(-90.74, -7.56) * mm});
            skPoint(sketch, "E84.middle", {"position": v(-83.62, 0) * mm});
            skLineSegment(sketch, "E85.bottom", {"start": v(-58.26, 7.37) * mm, "end": v(-72.49, 7.37) * mm});
            skLineSegment(sketch, "E85.top", {"start": v(-58.26, -7.37) * mm, "end": v(-72.49, -7.37) * mm});
            skLineSegment(sketch, "E85.left", {"start": v(-58.26, 7.37) * mm, "end": v(-58.26, -7.37) * mm});
            skLineSegment(sketch, "E85.right", {"start": v(-72.49, 7.37) * mm, "end": v(-72.49, -7.37) * mm});
            skPoint(sketch, "E85.middle", {"position": v(-65.37, 0) * mm});
            skLineSegment(sketch, "E86.bottom", {"start": v(-40.37, 7.56) * mm, "end": v(-55.34, 7.56) * mm});
            skLineSegment(sketch, "E86.top", {"start": v(-40.37, -7.56) * mm, "end": v(-55.34, -7.56) * mm});
            skLineSegment(sketch, "E86.left", {"start": v(-40.37, 7.56) * mm, "end": v(-40.37, -7.56) * mm});
            skLineSegment(sketch, "E86.right", {"start": v(-55.34, 7.56) * mm, "end": v(-55.34, -7.56) * mm});
            skPoint(sketch, "E86.middle", {"position": v(-47.86, 0) * mm});
            skLineSegment(sketch, "E87.bottom", {"start": v(-22.86, 7) * mm, "end": v(-37.09, 7) * mm});
            skLineSegment(sketch, "E87.top", {"start": v(-22.86, -7) * mm, "end": v(-37.09, -7) * mm});
            skLineSegment(sketch, "E87.left", {"start": v(-22.86, 7) * mm, "end": v(-22.86, -7) * mm});
            skLineSegment(sketch, "E87.right", {"start": v(-37.09, 7) * mm, "end": v(-37.09, -7) * mm});
            skPoint(sketch, "E87.middle", {"position": v(-29.97, 0) * mm});
            skLineSegment(sketch, "E88.bottom", {"start": v(-4.6, 7.2) * mm, "end": v(-19.21, 7.2) * mm});
            skLineSegment(sketch, "E88.top", {"start": v(-4.6, -7.2) * mm, "end": v(-19.21, -7.2) * mm});
            skLineSegment(sketch, "E88.left", {"start": v(-4.6, 7.2) * mm, "end": v(-4.6, -7.2) * mm});
            skLineSegment(sketch, "E88.right", {"start": v(-19.21, 7.2) * mm, "end": v(-19.21, -7.2) * mm});
            skPoint(sketch, "E88.middle", {"position": v(-11.9, 0) * mm});
            skLineSegment(sketch, "E89.bottom", {"start": v(13.46, 7) * mm, "end": v(-0.78, 7) * mm});
            skLineSegment(sketch, "E89.top", {"start": v(13.46, -7) * mm, "end": v(-0.78, -7) * mm});
            skLineSegment(sketch, "E89.left", {"start": v(13.46, 7) * mm, "end": v(13.46, -7) * mm});
            skLineSegment(sketch, "E89.right", {"start": v(-0.78, 7) * mm, "end": v(-0.78, -7) * mm});
            skPoint(sketch, "E89.middle", {"position": v(6.34, 0) * mm});
            skLineSegment(sketch, "E90.bottom", {"start": v(31.52, 7.2) * mm, "end": v(17.65, 7.2) * mm});
            skLineSegment(sketch, "E90.top", {"start": v(31.52, -7.2) * mm, "end": v(17.65, -7.2) * mm});
            skLineSegment(sketch, "E90.left", {"start": v(31.52, 7.2) * mm, "end": v(31.52, -7.2) * mm});
            skLineSegment(sketch, "E90.right", {"start": v(17.65, 7.2) * mm, "end": v(17.65, -7.2) * mm});
            skPoint(sketch, "E90.middle", {"position": v(24.59, 0) * mm});
            skLineSegment(sketch, "E91.bottom", {"start": v(49.77, 7) * mm, "end": v(35.54, 7) * mm});
            skLineSegment(sketch, "E91.top", {"start": v(49.77, -7) * mm, "end": v(35.54, -7) * mm});
            skLineSegment(sketch, "E91.left", {"start": v(49.77, 7) * mm, "end": v(49.77, -7) * mm});
            skLineSegment(sketch, "E91.right", {"start": v(35.54, 7) * mm, "end": v(35.54, -7) * mm});
            skPoint(sketch, "E91.middle", {"position": v(42.65, 0) * mm});
            skLineSegment(sketch, "E92.bottom", {"start": v(68.56, 7) * mm, "end": v(54.33, 7) * mm});
            skLineSegment(sketch, "E92.top", {"start": v(68.56, -7) * mm, "end": v(54.33, -7) * mm});
            skLineSegment(sketch, "E92.left", {"start": v(68.56, 7) * mm, "end": v(68.56, -7) * mm});
            skLineSegment(sketch, "E92.right", {"start": v(54.33, 7) * mm, "end": v(54.33, -7) * mm});
            skPoint(sketch, "E92.middle", {"position": v(61.45, 0) * mm});
            skLineSegment(sketch, "E93.bottom", {"start": v(68.38, 26.53) * mm, "end": v(54.88, 26.53) * mm});
            skLineSegment(sketch, "E93.top", {"start": v(68.38, 12.31) * mm, "end": v(54.88, 12.31) * mm});
            skLineSegment(sketch, "E93.left", {"start": v(68.38, 26.53) * mm, "end": v(68.38, 12.31) * mm});
            skLineSegment(sketch, "E93.right", {"start": v(54.88, 26.53) * mm, "end": v(54.88, 12.31) * mm});
            skPoint(sketch, "E93.middle", {"position": v(61.63, 19.42) * mm});
            skLineSegment(sketch, "E94.bottom", {"start": v(45.57, 26.72) * mm, "end": v(30.6, 26.72) * mm});
            skLineSegment(sketch, "E94.top", {"start": v(45.57, 12.13) * mm, "end": v(30.6, 12.13) * mm});
            skLineSegment(sketch, "E94.left", {"start": v(45.57, 26.72) * mm, "end": v(45.57, 12.13) * mm});
            skLineSegment(sketch, "E94.right", {"start": v(30.6, 26.72) * mm, "end": v(30.6, 12.13) * mm});
            skPoint(sketch, "E94.middle", {"position": v(38.1, 19.42) * mm});
            skLineSegment(sketch, "E95.bottom", {"start": v(27.1, 26.43) * mm, "end": v(13.29, 26.43) * mm});
            skLineSegment(sketch, "E95.top", {"start": v(27.1, 12.41) * mm, "end": v(13.29, 12.41) * mm});
            skLineSegment(sketch, "E95.left", {"start": v(27.1, 26.43) * mm, "end": v(27.1, 12.41) * mm});
            skLineSegment(sketch, "E95.right", {"start": v(13.29, 26.43) * mm, "end": v(13.29, 12.41) * mm});
            skPoint(sketch, "E95.middle", {"position": v(20.2, 19.42) * mm});
            skLineSegment(sketch, "E96.bottom", {"start": v(8.84, 26.36) * mm, "end": v(-4.66, 26.36) * mm});
            skLineSegment(sketch, "E96.top", {"start": v(8.84, 12.49) * mm, "end": v(-4.66, 12.49) * mm});
            skLineSegment(sketch, "E96.left", {"start": v(8.84, 26.36) * mm, "end": v(8.84, 12.49) * mm});
            skLineSegment(sketch, "E96.right", {"start": v(-4.66, 26.36) * mm, "end": v(-4.66, 12.49) * mm});
            skPoint(sketch, "E96.middle", {"position": v(2.09, 19.42) * mm});
            skLineSegment(sketch, "E97.bottom", {"start": v(-9.2, 26.36) * mm, "end": v(-23.61, 26.36) * mm});
            skLineSegment(sketch, "E97.top", {"start": v(-9.2, 12.49) * mm, "end": v(-23.61, 12.49) * mm});
            skLineSegment(sketch, "E97.left", {"start": v(-9.2, 26.36) * mm, "end": v(-9.2, 12.49) * mm});
            skLineSegment(sketch, "E97.right", {"start": v(-23.61, 26.36) * mm, "end": v(-23.61, 12.49) * mm});
            skPoint(sketch, "E97.middle", {"position": v(-16.4, 19.42) * mm});
            skLineSegment(sketch, "E98.bottom", {"start": v(-27.3, 26.43) * mm, "end": v(-41.26, 26.43) * mm});
            skLineSegment(sketch, "E98.top", {"start": v(-27.3, 12.41) * mm, "end": v(-41.26, 12.41) * mm});
            skLineSegment(sketch, "E98.left", {"start": v(-27.3, 26.43) * mm, "end": v(-27.3, 12.41) * mm});
            skLineSegment(sketch, "E98.right", {"start": v(-41.26, 26.43) * mm, "end": v(-41.26, 12.41) * mm});
            skPoint(sketch, "E98.middle", {"position": v(-34.28, 19.42) * mm});
            skLineSegment(sketch, "E99.bottom", {"start": v(-44.5, 26.94) * mm, "end": v(-59.28, 26.94) * mm});
            skLineSegment(sketch, "E99.top", {"start": v(-44.5, 11.9) * mm, "end": v(-59.28, 11.9) * mm});
            skLineSegment(sketch, "E99.left", {"start": v(-44.5, 26.94) * mm, "end": v(-44.5, 11.9) * mm});
            skLineSegment(sketch, "E99.right", {"start": v(-59.28, 26.94) * mm, "end": v(-59.28, 11.9) * mm});
            skPoint(sketch, "E99.middle", {"position": v(-51.9, 19.42) * mm});
            skLineSegment(sketch, "E100.bottom", {"start": v(-62.93, 26.58) * mm, "end": v(-77.35, 26.58) * mm});
            skLineSegment(sketch, "E100.top", {"start": v(-62.93, 12.26) * mm, "end": v(-77.35, 12.26) * mm});
            skLineSegment(sketch, "E100.left", {"start": v(-62.93, 26.58) * mm, "end": v(-62.93, 12.26) * mm});
            skLineSegment(sketch, "E100.right", {"start": v(-77.35, 26.58) * mm, "end": v(-77.35, 12.26) * mm});
            skPoint(sketch, "E100.middle", {"position": v(-70.14, 19.42) * mm});
            skLineSegment(sketch, "E101.bottom", {"start": v(-80.9, 26.58) * mm, "end": v(-96.23, 26.58) * mm});
            skLineSegment(sketch, "E101.top", {"start": v(-80.9, 12.26) * mm, "end": v(-96.23, 12.26) * mm});
            skLineSegment(sketch, "E101.left", {"start": v(-80.9, 26.58) * mm, "end": v(-80.9, 12.26) * mm});
            skLineSegment(sketch, "E101.right", {"start": v(-96.23, 26.58) * mm, "end": v(-96.23, 12.26) * mm});
            skPoint(sketch, "E101.middle", {"position": v(-88.57, 19.42) * mm});
            skLineSegment(sketch, "E102.bottom", {"start": v(-99.04, 26.43) * mm, "end": v(-113.93, 26.43) * mm});
            skLineSegment(sketch, "E102.top", {"start": v(-99.04, 12.42) * mm, "end": v(-113.93, 12.42) * mm});
            skLineSegment(sketch, "E102.left", {"start": v(-99.04, 26.43) * mm, "end": v(-99.04, 12.42) * mm});
            skLineSegment(sketch, "E102.right", {"start": v(-113.93, 26.43) * mm, "end": v(-113.93, 12.42) * mm});
            skPoint(sketch, "E102.middle", {"position": v(-106.48, 19.42) * mm});
            skLineSegment(sketch, "E103.bottom", {"start": v(-117.46, 26.8) * mm, "end": v(-131.73, 26.8) * mm});
            skLineSegment(sketch, "E103.top", {"start": v(-117.46, 12.03) * mm, "end": v(-131.73, 12.03) * mm});
            skLineSegment(sketch, "E103.left", {"start": v(-117.46, 26.8) * mm, "end": v(-117.46, 12.03) * mm});
            skLineSegment(sketch, "E103.right", {"start": v(-131.73, 26.8) * mm, "end": v(-131.73, 12.03) * mm});
            skPoint(sketch, "E103.middle", {"position": v(-124.6, 19.42) * mm});
            skLineSegment(sketch, "E104.bottom", {"start": v(-134.69, 26.58) * mm, "end": v(-150.34, 26.58) * mm});
            skLineSegment(sketch, "E104.top", {"start": v(-134.69, 12.26) * mm, "end": v(-150.34, 12.26) * mm});
            skLineSegment(sketch, "E104.left", {"start": v(-134.69, 26.58) * mm, "end": v(-134.69, 12.26) * mm});
            skLineSegment(sketch, "E104.right", {"start": v(-150.34, 26.58) * mm, "end": v(-150.34, 12.26) * mm});
            skPoint(sketch, "E104.middle", {"position": v(-142.51, 19.42) * mm});
            skLineSegment(sketch, "E105.bottom", {"start": v(-153.1, 26.5) * mm, "end": v(-168.3, 26.5) * mm});
            skLineSegment(sketch, "E105.top", {"start": v(-153.1, 12.54) * mm, "end": v(-168.3, 12.54) * mm});
            skLineSegment(sketch, "E105.left", {"start": v(-153.1, 26.5) * mm, "end": v(-153.1, 12.54) * mm});
            skLineSegment(sketch, "E105.right", {"start": v(-168.3, 26.5) * mm, "end": v(-168.3, 12.54) * mm});
            skPoint(sketch, "E105.middle", {"position": v(-160.7, 19.52) * mm});
            skLineSegment(sketch, "E106.bottom", {"start": v(-171.42, 26.13) * mm, "end": v(-186.46, 26.13) * mm});
            skLineSegment(sketch, "E106.top", {"start": v(-171.42, 12.71) * mm, "end": v(-186.46, 12.71) * mm});
            skLineSegment(sketch, "E106.left", {"start": v(-171.42, 26.13) * mm, "end": v(-171.42, 12.71) * mm});
            skLineSegment(sketch, "E106.right", {"start": v(-186.46, 26.13) * mm, "end": v(-186.46, 12.71) * mm});
            skPoint(sketch, "E106.middle", {"position": v(-178.94, 19.42) * mm});
            skLineSegment(sketch, "E107.bottom", {"start": v(-189.53, 26.6) * mm, "end": v(-204.56, 26.6) * mm});
            skLineSegment(sketch, "E107.top", {"start": v(-189.53, 12.48) * mm, "end": v(-204.56, 12.48) * mm});
            skLineSegment(sketch, "E107.left", {"start": v(-189.53, 26.6) * mm, "end": v(-189.53, 12.48) * mm});
            skLineSegment(sketch, "E107.right", {"start": v(-204.56, 26.6) * mm, "end": v(-204.56, 12.48) * mm});
            skPoint(sketch, "E107.middle", {"position": v(-197.05, 19.54) * mm});
            skLineSegment(sketch, "E108.bottom", {"start": v(-190.18, 45.02) * mm, "end": v(-204.93, 45.02) * mm});
            skLineSegment(sketch, "E108.top", {"start": v(-190.18, 60.17) * mm, "end": v(-204.93, 60.17) * mm});
            skLineSegment(sketch, "E108.left", {"start": v(-190.18, 45.02) * mm, "end": v(-190.18, 60.17) * mm});
            skLineSegment(sketch, "E108.right", {"start": v(-204.93, 45.02) * mm, "end": v(-204.93, 60.17) * mm});
            skPoint(sketch, "E108.middle", {"position": v(-197.56, 52.6) * mm});
            skLineSegment(sketch, "E109.bottom", {"start": v(-166.93, 45.17) * mm, "end": v(-181.2, 45.17) * mm});
            skLineSegment(sketch, "E109.top", {"start": v(-166.93, 60.02) * mm, "end": v(-181.2, 60.02) * mm});
            skLineSegment(sketch, "E109.left", {"start": v(-166.93, 45.17) * mm, "end": v(-166.93, 60.02) * mm});
            skLineSegment(sketch, "E109.right", {"start": v(-181.2, 45.17) * mm, "end": v(-181.2, 60.02) * mm});
            skPoint(sketch, "E109.middle", {"position": v(-174.07, 52.6) * mm});
            skLineSegment(sketch, "E110.bottom", {"start": v(-149.06, 44.86) * mm, "end": v(-162.87, 44.86) * mm});
            skLineSegment(sketch, "E110.top", {"start": v(-149.06, 60.32) * mm, "end": v(-162.87, 60.32) * mm});
            skLineSegment(sketch, "E110.left", {"start": v(-149.06, 44.86) * mm, "end": v(-149.06, 60.32) * mm});
            skLineSegment(sketch, "E110.right", {"start": v(-162.87, 44.86) * mm, "end": v(-162.87, 60.32) * mm});
            skPoint(sketch, "E110.middle", {"position": v(-155.96, 52.6) * mm});
            skLineSegment(sketch, "E111.bottom", {"start": v(-130.57, 44.71) * mm, "end": v(-144.84, 44.71) * mm});
            skLineSegment(sketch, "E111.top", {"start": v(-130.57, 60.48) * mm, "end": v(-144.84, 60.48) * mm});
            skLineSegment(sketch, "E111.left", {"start": v(-130.57, 44.71) * mm, "end": v(-130.57, 60.48) * mm});
            skLineSegment(sketch, "E111.right", {"start": v(-144.84, 44.71) * mm, "end": v(-144.84, 60.48) * mm});
            skPoint(sketch, "E111.middle", {"position": v(-137.7, 52.6) * mm});
            skLineSegment(sketch, "E112.bottom", {"start": v(-112.73, 44.74) * mm, "end": v(-127.61, 44.74) * mm});
            skLineSegment(sketch, "E112.top", {"start": v(-112.73, 60.45) * mm, "end": v(-127.61, 60.45) * mm});
            skLineSegment(sketch, "E112.left", {"start": v(-112.73, 44.74) * mm, "end": v(-112.73, 60.45) * mm});
            skLineSegment(sketch, "E112.right", {"start": v(-127.61, 44.74) * mm, "end": v(-127.61, 60.45) * mm});
            skPoint(sketch, "E112.middle", {"position": v(-120.17, 52.6) * mm});
            skLineSegment(sketch, "E113.bottom", {"start": v(-95.16, 44.74) * mm, "end": v(-109.43, 44.74) * mm});
            skLineSegment(sketch, "E113.top", {"start": v(-95.16, 60.45) * mm, "end": v(-109.43, 60.45) * mm});
            skLineSegment(sketch, "E113.left", {"start": v(-95.16, 44.74) * mm, "end": v(-95.16, 60.45) * mm});
            skLineSegment(sketch, "E113.right", {"start": v(-109.43, 44.74) * mm, "end": v(-109.43, 60.45) * mm});
            skPoint(sketch, "E113.middle", {"position": v(-102.3, 52.6) * mm});
            skLineSegment(sketch, "E114.bottom", {"start": v(-75.9, 44.97) * mm, "end": v(-90.94, 44.97) * mm});
            skLineSegment(sketch, "E114.top", {"start": v(-75.9, 60.22) * mm, "end": v(-90.94, 60.22) * mm});
            skLineSegment(sketch, "E114.left", {"start": v(-75.9, 44.97) * mm, "end": v(-75.9, 60.22) * mm});
            skLineSegment(sketch, "E114.right", {"start": v(-90.94, 44.97) * mm, "end": v(-90.94, 60.22) * mm});
            skPoint(sketch, "E114.middle", {"position": v(-83.42, 52.6) * mm});
            skLineSegment(sketch, "E115.bottom", {"start": v(-58.49, 45.08) * mm, "end": v(-73.07, 45.08) * mm});
            skLineSegment(sketch, "E115.top", {"start": v(-58.49, 60.1) * mm, "end": v(-73.07, 60.1) * mm});
            skLineSegment(sketch, "E115.left", {"start": v(-58.49, 45.08) * mm, "end": v(-58.49, 60.1) * mm});
            skLineSegment(sketch, "E115.right", {"start": v(-73.07, 45.08) * mm, "end": v(-73.07, 60.1) * mm});
            skPoint(sketch, "E115.middle", {"position": v(-65.78, 52.6) * mm});
            skLineSegment(sketch, "E116.bottom", {"start": v(-40.46, 44.85) * mm, "end": v(-55.34, 44.85) * mm});
            skLineSegment(sketch, "E116.top", {"start": v(-40.46, 60.33) * mm, "end": v(-55.34, 60.33) * mm});
            skLineSegment(sketch, "E116.left", {"start": v(-40.46, 44.85) * mm, "end": v(-40.46, 60.33) * mm});
            skLineSegment(sketch, "E116.right", {"start": v(-55.34, 44.85) * mm, "end": v(-55.34, 60.33) * mm});
            skPoint(sketch, "E116.middle", {"position": v(-47.9, 52.6) * mm});
            skLineSegment(sketch, "E117.bottom", {"start": v(-22.28, 45) * mm, "end": v(-37.31, 45) * mm});
            skLineSegment(sketch, "E117.top", {"start": v(-22.28, 60.18) * mm, "end": v(-37.31, 60.18) * mm});
            skLineSegment(sketch, "E117.left", {"start": v(-22.28, 45) * mm, "end": v(-22.28, 60.18) * mm});
            skLineSegment(sketch, "E117.right", {"start": v(-37.31, 45) * mm, "end": v(-37.31, 60.18) * mm});
            skPoint(sketch, "E117.middle", {"position": v(-29.8, 52.6) * mm});
            skLineSegment(sketch, "E118.bottom", {"start": v(-3.94, 45) * mm, "end": v(-19.13, 45) * mm});
            skLineSegment(sketch, "E118.top", {"start": v(-3.94, 60.18) * mm, "end": v(-19.13, 60.18) * mm});
            skLineSegment(sketch, "E118.left", {"start": v(-3.94, 45) * mm, "end": v(-3.94, 60.18) * mm});
            skLineSegment(sketch, "E118.right", {"start": v(-19.13, 45) * mm, "end": v(-19.13, 60.18) * mm});
            skPoint(sketch, "E118.middle", {"position": v(-11.53, 52.6) * mm});
            skLineSegment(sketch, "E119.bottom", {"start": v(13.34, 45.16) * mm, "end": v(-0.9, 45.16) * mm});
            skLineSegment(sketch, "E119.top", {"start": v(13.34, 60.03) * mm, "end": v(-0.9, 60.03) * mm});
            skLineSegment(sketch, "E119.left", {"start": v(13.34, 45.16) * mm, "end": v(13.34, 60.03) * mm});
            skLineSegment(sketch, "E119.right", {"start": v(-0.9, 45.16) * mm, "end": v(-0.9, 60.03) * mm});
            skPoint(sketch, "E119.middle", {"position": v(6.22, 52.6) * mm});
            skLineSegment(sketch, "E120.bottom", {"start": v(32.04, 45.34) * mm, "end": v(17.08, 45.34) * mm});
            skLineSegment(sketch, "E120.top", {"start": v(32.04, 59.85) * mm, "end": v(17.08, 59.85) * mm});
            skLineSegment(sketch, "E120.left", {"start": v(32.04, 45.34) * mm, "end": v(32.04, 59.85) * mm});
            skLineSegment(sketch, "E120.right", {"start": v(17.08, 45.34) * mm, "end": v(17.08, 59.85) * mm});
            skPoint(sketch, "E120.middle", {"position": v(24.56, 52.6) * mm});
            skLineSegment(sketch, "E121.bottom", {"start": v(54.12, 45.52) * mm, "end": v(39.89, 45.52) * mm});
            skLineSegment(sketch, "E121.top", {"start": v(54.12, 59.66) * mm, "end": v(39.89, 59.66) * mm});
            skLineSegment(sketch, "E121.left", {"start": v(54.12, 45.52) * mm, "end": v(54.12, 59.66) * mm});
            skLineSegment(sketch, "E121.right", {"start": v(39.89, 45.52) * mm, "end": v(39.89, 59.66) * mm});
            skPoint(sketch, "E121.middle", {"position": v(47, 52.6) * mm});
            skCircle(sketch, "E122", {"center": v(62.97, 57.57) * mm, "radius": 2.9 * mm});
            skCircle(sketch, "E123", {"center": v(62.79, 38.5) * mm, "radius": 2.9 * mm});
            skArc(sketch, "E124", {"start": v(136.73, -63.41) * mm, "mid": v(167.45, -65.88) * mm, "end": v(198.2, -63.72) * mm});
            skArc(sketch, "E125", {"start": v(136.73, -62.63) * mm, "mid": v(167.46, -63.88) * mm, "end": v(198.2, -62.68) * mm});
            skLineSegment(sketch, "E126", {"start": v(136.73, -62.63) * mm, "end": v(136.73, -63.41) * mm});
            skLineSegment(sketch, "E127", {"start": v(198.2, -62.68) * mm, "end": v(198.2, -63.72) * mm});
            skSolve(sketch);
        }
        {
            var Q0;
            Q0=makeQuery(id+"F0.imprint","IMPRINT",FACE,{"disambiguationData":[TD([[makeQuery(id+"F0.imprint","IMPRINT",EDGE,{"derivedFrom":sQuery(id+"F0.wireOp",EDGE,"E15.bottom")}),1.0]])]});
            var Q1;
            Q1=makeQuery(id+"F0.imprint","IMPRINT",FACE,{"disambiguationData":[TD([[makeQuery(id+"F0.imprint","IMPRINT",EDGE,{"derivedFrom":sQuery(id+"F0.wireOp",EDGE,"E45.bottom")}),1.0]])]});
            var Q2;
            Q2=makeQuery(id+"F0.imprint","IMPRINT",FACE,{"disambiguationData":[TD([[makeQuery(id+"F0.imprint","IMPRINT",EDGE,{"derivedFrom":sQuery(id+"F0.wireOp",EDGE,"E77.bottom")}),1.0]])]});
            var Q3;
            Q3=makeQuery(id+"F0.imprint","IMPRINT",FACE,{"disambiguationData":[TD([[makeQuery(id+"F0.imprint","IMPRINT",EDGE,{"derivedFrom":sQuery(id+"F0.wireOp",EDGE,"E65.bottom")}),1.0]])]});
            var Q4;
            Q4=makeQuery(id+"F0.imprint","IMPRINT",FACE,{"disambiguationData":[TD([[makeQuery(id+"F0.imprint","IMPRINT",EDGE,{"derivedFrom":sQuery(id+"F0.wireOp",EDGE,"E0.bottom")}),1.0]])]});
            var Q5;
            Q5=makeQuery(id+"F0.imprint","IMPRINT",FACE,{"disambiguationData":[TD([[makeQuery(id+"F0.imprint","IMPRINT",EDGE,{"derivedFrom":sQuery(id+"F0.wireOp",EDGE,"E78.bottom")}),1.0]])]});
            var Q6;
            Q6=makeQuery(id+"F0.imprint","IMPRINT",FACE,{"disambiguationData":[TD([[makeQuery(id+"F0.imprint","IMPRINT",EDGE,{"derivedFrom":sQuery(id+"F0.wireOp",EDGE,"E28.bottom")}),1.0]])]});
            var Q7;
            Q7=makeQuery(id+"F0.imprint","IMPRINT",FACE,{"disambiguationData":[TD([[makeQuery(id+"F0.imprint","IMPRINT",EDGE,{"derivedFrom":sQuery(id+"F0.wireOp",EDGE,"E48.bottom")}),1.0]])]});
            var Q8;
            Q8=makeQuery(id+"F0.imprint","IMPRINT",FACE,{"disambiguationData":[TD([[makeQuery(id+"F0.imprint","IMPRINT",EDGE,{"derivedFrom":sQuery(id+"F0.wireOp",EDGE,"E69.bottom")}),1.0]])]});
            var Q9;
            Q9=makeQuery(id+"F0.imprint","IMPRINT",FACE,{"disambiguationData":[TD([[makeQuery(id+"F0.imprint","IMPRINT",EDGE,{"derivedFrom":sQuery(id+"F0.wireOp",EDGE,"E99.bottom")}),1.0]])]});
            var Q10;
            Q10=makeQuery(id+"F0.imprint","IMPRINT",FACE,{"disambiguationData":[TD([[makeQuery(id+"F0.imprint","IMPRINT",EDGE,{"derivedFrom":sQuery(id+"F0.wireOp",EDGE,"E60.bottom")}),1.0]])]});
            var Q11;
            Q11=makeQuery(id+"F0.imprint","IMPRINT",FACE,{"disambiguationData":[TD([[makeQuery(id+"F0.imprint","IMPRINT",EDGE,{"derivedFrom":sQuery(id+"F0.wireOp",EDGE,"E68.bottom")}),1.0]])]});
            var Q12;
            Q12=makeQuery(id+"F0.imprint","IMPRINT",FACE,{"disambiguationData":[TD([[makeQuery(id+"F0.imprint","IMPRINT",EDGE,{"derivedFrom":sQuery(id+"F0.wireOp",EDGE,"E90.bottom")}),1.0]])]});
            var Q13;
            Q13=makeQuery(id+"F0.imprint","IMPRINT",FACE,{"disambiguationData":[TD([[makeQuery(id+"F0.imprint","IMPRINT",EDGE,{"derivedFrom":sQuery(id+"F0.wireOp",EDGE,"E122")}),1.0]])]});
            var Q14;
            Q14=makeQuery(id+"F0.imprint","IMPRINT",FACE,{"disambiguationData":[TD([[makeQuery(id+"F0.imprint","IMPRINT",EDGE,{"derivedFrom":sQuery(id+"F0.wireOp",EDGE,"E111.bottom")}),-1.0]])]});
            var Q15;
            Q15=makeQuery(id+"F0.imprint","IMPRINT",FACE,{"disambiguationData":[TD([[makeQuery(id+"F0.imprint","IMPRINT",EDGE,{"derivedFrom":sQuery(id+"F0.wireOp",EDGE,"E110.bottom")}),-1.0]])]});
            var Q16;
            Q16=makeQuery(id+"F0.imprint","IMPRINT",FACE,{"disambiguationData":[TD([[makeQuery(id+"F0.imprint","IMPRINT",EDGE,{"derivedFrom":sQuery(id+"F0.wireOp",EDGE,"E80.bottom")}),1.0]])]});
            var Q17;
            Q17=makeQuery(id+"F0.imprint","IMPRINT",FACE,{"disambiguationData":[TD([[makeQuery(id+"F0.imprint","IMPRINT",EDGE,{"derivedFrom":sQuery(id+"F0.wireOp",EDGE,"E25.bottom")}),1.0]])]});
            var Q18;
            Q18=makeQuery(id+"F0.imprint","IMPRINT",FACE,{"disambiguationData":[TD([[makeQuery(id+"F0.imprint","IMPRINT",EDGE,{"derivedFrom":sQuery(id+"F0.wireOp",EDGE,"E52.bottom")}),1.0]])]});
            var Q19;
            Q19=makeQuery(id+"F0.imprint","IMPRINT",FACE,{"disambiguationData":[TD([[makeQuery(id+"F0.imprint","IMPRINT",EDGE,{"derivedFrom":sQuery(id+"F0.wireOp",EDGE,"E91.bottom")}),1.0]])]});
            var Q20;
            Q20=makeQuery(id+"F0.imprint","IMPRINT",FACE,{"disambiguationData":[TD([[makeQuery(id+"F0.imprint","IMPRINT",EDGE,{"derivedFrom":sQuery(id+"F0.wireOp",EDGE,"E82.bottom")}),1.0]])]});
            var Q21;
            Q21=makeQuery(id+"F0.imprint","IMPRINT",FACE,{"disambiguationData":[TD([[makeQuery(id+"F0.imprint","IMPRINT",EDGE,{"derivedFrom":sQuery(id+"F0.wireOp",EDGE,"E85.bottom")}),1.0]])]});
            var Q22;
            Q22=makeQuery(id+"F0.imprint","IMPRINT",FACE,{"disambiguationData":[TD([[makeQuery(id+"F0.imprint","IMPRINT",EDGE,{"derivedFrom":sQuery(id+"F0.wireOp",EDGE,"E88.bottom")}),1.0]])]});
            var Q23;
            Q23=makeQuery(id+"F0.imprint","IMPRINT",FACE,{"disambiguationData":[TD([[makeQuery(id+"F0.imprint","IMPRINT",EDGE,{"derivedFrom":sQuery(id+"F0.wireOp",EDGE,"E105.bottom")}),1.0]])]});
            var Q24;
            Q24=makeQuery(id+"F0.imprint","IMPRINT",FACE,{"disambiguationData":[TD([[makeQuery(id+"F0.imprint","IMPRINT",EDGE,{"derivedFrom":sQuery(id+"F0.wireOp",EDGE,"E16.bottom")}),1.0]])]});
            var Q25;
            Q25=makeQuery(id+"F0.imprint","IMPRINT",FACE,{"disambiguationData":[TD([[makeQuery(id+"F0.imprint","IMPRINT",EDGE,{"derivedFrom":sQuery(id+"F0.wireOp",EDGE,"E42.bottom")}),1.0]])]});
            var Q26;
            Q26=makeQuery(id+"F0.imprint","IMPRINT",FACE,{"disambiguationData":[TD([[makeQuery(id+"F0.imprint","IMPRINT",EDGE,{"derivedFrom":sQuery(id+"F0.wireOp",EDGE,"E44.bottom")}),1.0]])]});
            var Q27;
            Q27=makeQuery(id+"F0.imprint","IMPRINT",FACE,{"disambiguationData":[TD([[makeQuery(id+"F0.imprint","IMPRINT",EDGE,{"derivedFrom":sQuery(id+"F0.wireOp",EDGE,"E118.bottom")}),-1.0]])]});
            var Q28;
            Q28=makeQuery(id+"F0.imprint","IMPRINT",FACE,{"disambiguationData":[TD([[makeQuery(id+"F0.imprint","IMPRINT",EDGE,{"derivedFrom":sQuery(id+"F0.wireOp",EDGE,"E109.bottom")}),-1.0]])]});
            var Q29;
            Q29=makeQuery(id+"F0.imprint","IMPRINT",FACE,{"disambiguationData":[TD([[makeQuery(id+"F0.imprint","IMPRINT",EDGE,{"derivedFrom":sQuery(id+"F0.wireOp",EDGE,"E86.bottom")}),1.0]])]});
            var Q30;
            Q30=makeQuery(id+"F0.imprint","IMPRINT",FACE,{"disambiguationData":[TD([[makeQuery(id+"F0.imprint","IMPRINT",EDGE,{"derivedFrom":sQuery(id+"F0.wireOp",EDGE,"E26.bottom")}),1.0]])]});
            var Q31;
            Q31=makeQuery(id+"F0.imprint","IMPRINT",FACE,{"disambiguationData":[TD([[makeQuery(id+"F0.imprint","IMPRINT",EDGE,{"derivedFrom":sQuery(id+"F0.wireOp",EDGE,"E23.bottom")}),1.0]])]});
            var Q32;
            Q32=makeQuery(id+"F0.imprint","IMPRINT",FACE,{"disambiguationData":[TD([[makeQuery(id+"F0.imprint","IMPRINT",EDGE,{"derivedFrom":sQuery(id+"F0.wireOp",EDGE,"E101.bottom")}),1.0]])]});
            var Q33;
            Q33=makeQuery(id+"F0.imprint","IMPRINT",FACE,{"disambiguationData":[TD([[makeQuery(id+"F0.imprint","IMPRINT",EDGE,{"derivedFrom":sQuery(id+"F0.wireOp",EDGE,"E73.bottom")}),1.0]])]});
            var Q34;
            Q34=makeQuery(id+"F0.imprint","IMPRINT",FACE,{"disambiguationData":[TD([[makeQuery(id+"F0.imprint","IMPRINT",EDGE,{"derivedFrom":sQuery(id+"F0.wireOp",EDGE,"E58.bottom")}),1.0]])]});
            var Q35;
            Q35=makeQuery(id+"F0.imprint","IMPRINT",FACE,{"disambiguationData":[TD([[makeQuery(id+"F0.imprint","IMPRINT",EDGE,{"derivedFrom":sQuery(id+"F0.wireOp",EDGE,"E123")}),1.0]])]});
            var Q36;
            Q36=makeQuery(id+"F0.imprint","IMPRINT",FACE,{"disambiguationData":[TD([[makeQuery(id+"F0.imprint","IMPRINT",EDGE,{"derivedFrom":sQuery(id+"F0.wireOp",EDGE,"E95.bottom")}),1.0]])]});
            var Q37;
            Q37=makeQuery(id+"F0.imprint","IMPRINT",FACE,{"disambiguationData":[TD([[makeQuery(id+"F0.imprint","IMPRINT",EDGE,{"derivedFrom":sQuery(id+"F0.wireOp",EDGE,"E93.bottom")}),1.0]])]});
            var Q38;
            Q38=makeQuery(id+"F0.imprint","IMPRINT",FACE,{"disambiguationData":[TD([[makeQuery(id+"F0.imprint","IMPRINT",EDGE,{"derivedFrom":sQuery(id+"F0.wireOp",EDGE,"E81.bottom")}),1.0]])]});
            var Q39;
            Q39=makeQuery(id+"F0.imprint","IMPRINT",FACE,{"disambiguationData":[TD([[makeQuery(id+"F0.imprint","IMPRINT",EDGE,{"derivedFrom":sQuery(id+"F0.wireOp",EDGE,"E114.bottom")}),-1.0]])]});
            var Q40;
            Q40=makeQuery(id+"F0.imprint","IMPRINT",FACE,{"disambiguationData":[TD([[makeQuery(id+"F0.imprint","IMPRINT",EDGE,{"derivedFrom":sQuery(id+"F0.wireOp",EDGE,"E22.bottom")}),1.0]])]});
            var Q41;
            Q41=makeQuery(id+"F0.imprint","IMPRINT",FACE,{"disambiguationData":[TD([[makeQuery(id+"F0.imprint","IMPRINT",EDGE,{"derivedFrom":sQuery(id+"F0.wireOp",EDGE,"E67.bottom")}),1.0]])]});
            var Q42;
            Q42=makeQuery(id+"F0.imprint","IMPRINT",FACE,{"disambiguationData":[TD([[makeQuery(id+"F0.imprint","IMPRINT",EDGE,{"derivedFrom":sQuery(id+"F0.wireOp",EDGE,"E40.bottom")}),1.0]])]});
            var Q43;
            Q43=makeQuery(id+"F0.imprint","IMPRINT",FACE,{"disambiguationData":[TD([[makeQuery(id+"F0.imprint","IMPRINT",EDGE,{"derivedFrom":sQuery(id+"F0.wireOp",EDGE,"E62.bottom")}),1.0]])]});
            var Q44;
            Q44=makeQuery(id+"F0.imprint","IMPRINT",FACE,{"disambiguationData":[TD([[makeQuery(id+"F0.imprint","IMPRINT",EDGE,{"derivedFrom":sQuery(id+"F0.wireOp",EDGE,"E74.bottom")}),1.0]])]});
            var Q45;
            Q45=makeQuery(id+"F0.imprint","IMPRINT",FACE,{"disambiguationData":[TD([[makeQuery(id+"F0.imprint","IMPRINT",EDGE,{"derivedFrom":sQuery(id+"F0.wireOp",EDGE,"E20.bottom")}),1.0]])]});
            var Q46;
            Q46=makeQuery(id+"F0.imprint","IMPRINT",FACE,{"disambiguationData":[TD([[makeQuery(id+"F0.imprint","IMPRINT",EDGE,{"derivedFrom":sQuery(id+"F0.wireOp",EDGE,"E56.bottom")}),1.0]])]});
            var Q47;
            Q47=makeQuery(id+"F0.imprint","IMPRINT",FACE,{"disambiguationData":[TD([[makeQuery(id+"F0.imprint","IMPRINT",EDGE,{"derivedFrom":sQuery(id+"F0.wireOp",EDGE,"E54.bottom")}),1.0]])]});
            var Q48;
            Q48=makeQuery(id+"F0.imprint","IMPRINT",FACE,{"disambiguationData":[TD([[makeQuery(id+"F0.imprint","IMPRINT",EDGE,{"derivedFrom":sQuery(id+"F0.wireOp",EDGE,"E75.bottom")}),1.0]])]});
            var Q49;
            Q49=makeQuery(id+"F0.imprint","IMPRINT",FACE,{"disambiguationData":[TD([[makeQuery(id+"F0.imprint","IMPRINT",EDGE,{"derivedFrom":sQuery(id+"F0.wireOp",EDGE,"E120.bottom")}),-1.0]])]});
            var Q50;
            Q50=makeQuery(id+"F0.imprint","IMPRINT",FACE,{"disambiguationData":[TD([[makeQuery(id+"F0.imprint","IMPRINT",EDGE,{"derivedFrom":sQuery(id+"F0.wireOp",EDGE,"E61.bottom")}),1.0]])]});
            var Q51;
            Q51=makeQuery(id+"F0.imprint","IMPRINT",FACE,{"disambiguationData":[TD([[makeQuery(id+"F0.imprint","IMPRINT",EDGE,{"derivedFrom":sQuery(id+"F0.wireOp",EDGE,"E66.bottom")}),1.0]])]});
            var Q52;
            Q52=makeQuery(id+"F0.imprint","IMPRINT",FACE,{"disambiguationData":[TD([[makeQuery(id+"F0.imprint","IMPRINT",EDGE,{"derivedFrom":sQuery(id+"F0.wireOp",EDGE,"E43.bottom")}),1.0]])]});
            var Q53;
            Q53=makeQuery(id+"F0.imprint","IMPRINT",FACE,{"disambiguationData":[TD([[makeQuery(id+"F0.imprint","IMPRINT",EDGE,{"derivedFrom":sQuery(id+"F0.wireOp",EDGE,"E50.bottom")}),1.0]])]});
            var Q54;
            Q54=makeQuery(id+"F0.imprint","IMPRINT",FACE,{"disambiguationData":[TD([[makeQuery(id+"F0.imprint","IMPRINT",EDGE,{"derivedFrom":sQuery(id+"F0.wireOp",EDGE,"E17.bottom")}),1.0]])]});
            var Q55;
            Q55=makeQuery(id+"F0.imprint","IMPRINT",FACE,{"disambiguationData":[TD([[makeQuery(id+"F0.imprint","IMPRINT",EDGE,{"derivedFrom":sQuery(id+"F0.wireOp",EDGE,"E19.bottom")}),1.0]])]});
            var Q56;
            Q56=makeQuery(id+"F0.imprint","IMPRINT",FACE,{"disambiguationData":[TD([[makeQuery(id+"F0.imprint","IMPRINT",EDGE,{"derivedFrom":sQuery(id+"F0.wireOp",EDGE,"E30.bottom")}),1.0]])]});
            var Q57;
            Q57=makeQuery(id+"F0.imprint","IMPRINT",FACE,{"disambiguationData":[TD([[makeQuery(id+"F0.imprint","IMPRINT",EDGE,{"derivedFrom":sQuery(id+"F0.wireOp",EDGE,"E106.bottom")}),1.0]])]});
            var Q58;
            Q58=makeQuery(id+"F0.imprint","IMPRINT",FACE,{"disambiguationData":[TD([[makeQuery(id+"F0.imprint","IMPRINT",EDGE,{"derivedFrom":sQuery(id+"F0.wireOp",EDGE,"E64.bottom")}),1.0]])]});
            var Q59;
            Q59=makeQuery(id+"F0.imprint","IMPRINT",FACE,{"disambiguationData":[TD([[makeQuery(id+"F0.imprint","IMPRINT",EDGE,{"derivedFrom":sQuery(id+"F0.wireOp",EDGE,"E124")}),1.0]])]});
            var Q60;
            Q60=makeQuery(id+"F0.imprint","IMPRINT",FACE,{"disambiguationData":[TD([[makeQuery(id+"F0.imprint","IMPRINT",EDGE,{"derivedFrom":sQuery(id+"F0.wireOp",EDGE,"E97.bottom")}),1.0]])]});
            var Q61;
            Q61=makeQuery(id+"F0.imprint","IMPRINT",FACE,{"disambiguationData":[TD([[makeQuery(id+"F0.imprint","IMPRINT",EDGE,{"derivedFrom":sQuery(id+"F0.wireOp",EDGE,"E36.bottom")}),1.0]])]});
            var Q62;
            Q62=makeQuery(id+"F0.imprint","IMPRINT",FACE,{"disambiguationData":[TD([[makeQuery(id+"F0.imprint","IMPRINT",EDGE,{"derivedFrom":sQuery(id+"F0.wireOp",EDGE,"E49.bottom")}),1.0]])]});
            var Q63;
            Q63=makeQuery(id+"F0.imprint","IMPRINT",FACE,{"disambiguationData":[TD([[makeQuery(id+"F0.imprint","IMPRINT",EDGE,{"derivedFrom":sQuery(id+"F0.wireOp",EDGE,"E34.bottom")}),1.0]])]});
            var Q64;
            Q64=makeQuery(id+"F0.imprint","IMPRINT",FACE,{"disambiguationData":[TD([[makeQuery(id+"F0.imprint","IMPRINT",EDGE,{"derivedFrom":sQuery(id+"F0.wireOp",EDGE,"E18.bottom")}),1.0]])]});
            var Q65;
            Q65=makeQuery(id+"F0.imprint","IMPRINT",FACE,{"disambiguationData":[TD([[makeQuery(id+"F0.imprint","IMPRINT",EDGE,{"derivedFrom":sQuery(id+"F0.wireOp",EDGE,"E59.bottom")}),1.0]])]});
            var Q66;
            Q66=makeQuery(id+"F0.imprint","IMPRINT",FACE,{"disambiguationData":[TD([[makeQuery(id+"F0.imprint","IMPRINT",EDGE,{"derivedFrom":sQuery(id+"F0.wireOp",EDGE,"E35.bottom")}),1.0]])]});
            var Q67;
            Q67=makeQuery(id+"F0.imprint","IMPRINT",FACE,{"disambiguationData":[TD([[makeQuery(id+"F0.imprint","IMPRINT",EDGE,{"derivedFrom":sQuery(id+"F0.wireOp",EDGE,"E107.bottom")}),1.0]])]});
            var Q68;
            Q68=makeQuery(id+"F0.imprint","IMPRINT",FACE,{"disambiguationData":[TD([[makeQuery(id+"F0.imprint","IMPRINT",EDGE,{"derivedFrom":sQuery(id+"F0.wireOp",EDGE,"E104.bottom")}),1.0]])]});
            var Q69;
            Q69=makeQuery(id+"F0.imprint","IMPRINT",FACE,{"disambiguationData":[TD([[makeQuery(id+"F0.imprint","IMPRINT",EDGE,{"derivedFrom":sQuery(id+"F0.wireOp",EDGE,"E55.bottom")}),1.0]])]});
            var Q70;
            Q70=makeQuery(id+"F0.imprint","IMPRINT",FACE,{"disambiguationData":[TD([[makeQuery(id+"F0.imprint","IMPRINT",EDGE,{"derivedFrom":sQuery(id+"F0.wireOp",EDGE,"E46.bottom")}),1.0]])]});
            var Q71;
            Q71=makeQuery(id+"F0.imprint","IMPRINT",FACE,{"disambiguationData":[TD([[makeQuery(id+"F0.imprint","IMPRINT",EDGE,{"derivedFrom":sQuery(id+"F0.wireOp",EDGE,"E94.bottom")}),1.0]])]});
            var Q72;
            Q72=makeQuery(id+"F0.imprint","IMPRINT",FACE,{"disambiguationData":[TD([[makeQuery(id+"F0.imprint","IMPRINT",EDGE,{"derivedFrom":sQuery(id+"F0.wireOp",EDGE,"E102.bottom")}),1.0]])]});
            var Q73;
            Q73=makeQuery(id+"F0.imprint","IMPRINT",FACE,{"disambiguationData":[TD([[makeQuery(id+"F0.imprint","IMPRINT",EDGE,{"derivedFrom":sQuery(id+"F0.wireOp",EDGE,"E39.bottom")}),1.0]])]});
            var Q74;
            Q74=makeQuery(id+"F0.imprint","IMPRINT",FACE,{"disambiguationData":[TD([[makeQuery(id+"F0.imprint","IMPRINT",EDGE,{"derivedFrom":sQuery(id+"F0.wireOp",EDGE,"E47.bottom")}),1.0]])]});
            var Q75;
            Q75=makeQuery(id+"F0.imprint","IMPRINT",FACE,{"disambiguationData":[TD([[makeQuery(id+"F0.imprint","IMPRINT",EDGE,{"derivedFrom":sQuery(id+"F0.wireOp",EDGE,"E115.bottom")}),-1.0]])]});
            var Q76;
            Q76=makeQuery(id+"F0.imprint","IMPRINT",FACE,{"disambiguationData":[TD([[makeQuery(id+"F0.imprint","IMPRINT",EDGE,{"derivedFrom":sQuery(id+"F0.wireOp",EDGE,"E117.bottom")}),-1.0]])]});
            var Q77;
            Q77=makeQuery(id+"F0.imprint","IMPRINT",FACE,{"disambiguationData":[TD([[makeQuery(id+"F0.imprint","IMPRINT",EDGE,{"derivedFrom":sQuery(id+"F0.wireOp",EDGE,"E89.bottom")}),1.0]])]});
            var Q78;
            Q78=makeQuery(id+"F0.imprint","IMPRINT",FACE,{"disambiguationData":[TD([[makeQuery(id+"F0.imprint","IMPRINT",EDGE,{"derivedFrom":sQuery(id+"F0.wireOp",EDGE,"E119.bottom")}),-1.0]])]});
            var Q79;
            Q79=makeQuery(id+"F0.imprint","IMPRINT",FACE,{"disambiguationData":[TD([[makeQuery(id+"F0.imprint","IMPRINT",EDGE,{"derivedFrom":sQuery(id+"F0.wireOp",EDGE,"E87.bottom")}),1.0]])]});
            var Q80;
            Q80=makeQuery(id+"F0.imprint","IMPRINT",FACE,{"disambiguationData":[TD([[makeQuery(id+"F0.imprint","IMPRINT",EDGE,{"derivedFrom":sQuery(id+"F0.wireOp",EDGE,"E76.bottom")}),1.0]])]});
            var Q81;
            Q81=makeQuery(id+"F0.imprint","IMPRINT",FACE,{"disambiguationData":[TD([[makeQuery(id+"F0.imprint","IMPRINT",EDGE,{"derivedFrom":sQuery(id+"F0.wireOp",EDGE,"E72.bottom")}),1.0]])]});
            var Q82;
            Q82=makeQuery(id+"F0.imprint","IMPRINT",FACE,{"disambiguationData":[TD([[makeQuery(id+"F0.imprint","IMPRINT",EDGE,{"derivedFrom":sQuery(id+"F0.wireOp",EDGE,"E63.bottom")}),1.0]])]});
            var Q83;
            Q83=makeQuery(id+"F0.imprint","IMPRINT",FACE,{"disambiguationData":[TD([[makeQuery(id+"F0.imprint","IMPRINT",EDGE,{"derivedFrom":sQuery(id+"F0.wireOp",EDGE,"E33.bottom")}),1.0]])]});
            var Q84;
            Q84=makeQuery(id+"F0.imprint","IMPRINT",FACE,{"disambiguationData":[TD([[makeQuery(id+"F0.imprint","IMPRINT",EDGE,{"derivedFrom":sQuery(id+"F0.wireOp",EDGE,"E92.bottom")}),1.0]])]});
            var Q85;
            Q85=makeQuery(id+"F0.imprint","IMPRINT",FACE,{"disambiguationData":[TD([[makeQuery(id+"F0.imprint","IMPRINT",EDGE,{"derivedFrom":sQuery(id+"F0.wireOp",EDGE,"E100.bottom")}),1.0]])]});
            var Q86;
            Q86=makeQuery(id+"F0.imprint","IMPRINT",FACE,{"disambiguationData":[TD([[makeQuery(id+"F0.imprint","IMPRINT",EDGE,{"derivedFrom":sQuery(id+"F0.wireOp",EDGE,"E38.bottom")}),1.0]])]});
            var Q87;
            Q87=makeQuery(id+"F0.imprint","IMPRINT",FACE,{"disambiguationData":[TD([[makeQuery(id+"F0.imprint","IMPRINT",EDGE,{"derivedFrom":sQuery(id+"F0.wireOp",EDGE,"E37.bottom")}),1.0]])]});
            var Q88;
            Q88=makeQuery(id+"F0.imprint","IMPRINT",FACE,{"disambiguationData":[TD([[makeQuery(id+"F0.imprint","IMPRINT",EDGE,{"derivedFrom":sQuery(id+"F0.wireOp",EDGE,"E31.bottom")}),1.0]])]});
            var Q89;
            Q89=makeQuery(id+"F0.imprint","IMPRINT",FACE,{"disambiguationData":[TD([[makeQuery(id+"F0.imprint","IMPRINT",EDGE,{"derivedFrom":sQuery(id+"F0.wireOp",EDGE,"E70.bottom")}),1.0]])]});
            var Q90;
            Q90=makeQuery(id+"F0.imprint","IMPRINT",FACE,{"disambiguationData":[TD([[makeQuery(id+"F0.imprint","IMPRINT",EDGE,{"derivedFrom":sQuery(id+"F0.wireOp",EDGE,"E112.bottom")}),-1.0]])]});
            var Q91;
            Q91=makeQuery(id+"F0.imprint","IMPRINT",FACE,{"disambiguationData":[TD([[makeQuery(id+"F0.imprint","IMPRINT",EDGE,{"derivedFrom":sQuery(id+"F0.wireOp",EDGE,"E83.bottom")}),1.0]])]});
            var Q92;
            Q92=makeQuery(id+"F0.imprint","IMPRINT",FACE,{"disambiguationData":[TD([[makeQuery(id+"F0.imprint","IMPRINT",EDGE,{"derivedFrom":sQuery(id+"F0.wireOp",EDGE,"E32.bottom")}),1.0]])]});
            var Q93;
            Q93=makeQuery(id+"F0.imprint","IMPRINT",FACE,{"disambiguationData":[TD([[makeQuery(id+"F0.imprint","IMPRINT",EDGE,{"derivedFrom":sQuery(id+"F0.wireOp",EDGE,"E29.bottom")}),1.0]])]});
            var Q94;
            Q94=makeQuery(id+"F0.imprint","IMPRINT",FACE,{"disambiguationData":[TD([[makeQuery(id+"F0.imprint","IMPRINT",EDGE,{"derivedFrom":sQuery(id+"F0.wireOp",EDGE,"E57.bottom")}),1.0]])]});
            var Q95;
            Q95=makeQuery(id+"F0.imprint","IMPRINT",FACE,{"disambiguationData":[TD([[makeQuery(id+"F0.imprint","IMPRINT",EDGE,{"derivedFrom":sQuery(id+"F0.wireOp",EDGE,"E51.bottom")}),1.0]])]});
            var Q96;
            Q96=makeQuery(id+"F0.imprint","IMPRINT",FACE,{"disambiguationData":[TD([[makeQuery(id+"F0.imprint","IMPRINT",EDGE,{"derivedFrom":sQuery(id+"F0.wireOp",EDGE,"E71.bottom")}),1.0]])]});
            var Q97;
            Q97=makeQuery(id+"F0.imprint","IMPRINT",FACE,{"disambiguationData":[TD([[makeQuery(id+"F0.imprint","IMPRINT",EDGE,{"derivedFrom":sQuery(id+"F0.wireOp",EDGE,"E98.bottom")}),1.0]])]});
            var Q98;
            Q98=makeQuery(id+"F0.imprint","IMPRINT",FACE,{"disambiguationData":[TD([[makeQuery(id+"F0.imprint","IMPRINT",EDGE,{"derivedFrom":sQuery(id+"F0.wireOp",EDGE,"E103.bottom")}),1.0]])]});
            var Q99;
            Q99=makeQuery(id+"F0.imprint","IMPRINT",FACE,{"disambiguationData":[TD([[makeQuery(id+"F0.imprint","IMPRINT",EDGE,{"derivedFrom":sQuery(id+"F0.wireOp",EDGE,"E41.bottom")}),1.0]])]});
            var Q100;
            Q100=makeQuery(id+"F0.imprint","IMPRINT",FACE,{"disambiguationData":[TD([[makeQuery(id+"F0.imprint","IMPRINT",EDGE,{"derivedFrom":sQuery(id+"F0.wireOp",EDGE,"E108.bottom")}),-1.0]])]});
            var Q101;
            Q101=makeQuery(id+"F0.imprint","IMPRINT",FACE,{"disambiguationData":[TD([[makeQuery(id+"F0.imprint","IMPRINT",EDGE,{"derivedFrom":sQuery(id+"F0.wireOp",EDGE,"E53.bottom")}),1.0]])]});
            var Q102;
            Q102=makeQuery(id+"F0.imprint","IMPRINT",FACE,{"disambiguationData":[TD([[makeQuery(id+"F0.imprint","IMPRINT",EDGE,{"derivedFrom":sQuery(id+"F0.wireOp",EDGE,"E21.bottom")}),1.0]])]});
            var Q103;
            Q103=makeQuery(id+"F0.imprint","IMPRINT",FACE,{"disambiguationData":[TD([[makeQuery(id+"F0.imprint","IMPRINT",EDGE,{"derivedFrom":sQuery(id+"F0.wireOp",EDGE,"E27.bottom")}),1.0]])]});
            var Q104;
            Q104=makeQuery(id+"F0.imprint","IMPRINT",FACE,{"disambiguationData":[TD([[makeQuery(id+"F0.imprint","IMPRINT",EDGE,{"derivedFrom":sQuery(id+"F0.wireOp",EDGE,"E79.bottom")}),1.0]])]});
            var Q105;
            Q105=makeQuery(id+"F0.imprint","IMPRINT",FACE,{"disambiguationData":[TD([[makeQuery(id+"F0.imprint","IMPRINT",EDGE,{"derivedFrom":sQuery(id+"F0.wireOp",EDGE,"E113.bottom")}),-1.0]])]});
            var Q106;
            Q106=makeQuery(id+"F0.imprint","IMPRINT",FACE,{"disambiguationData":[TD([[makeQuery(id+"F0.imprint","IMPRINT",EDGE,{"derivedFrom":sQuery(id+"F0.wireOp",EDGE,"E121.bottom")}),-1.0]])]});
            var Q107;
            Q107=makeQuery(id+"F0.imprint","IMPRINT",FACE,{"disambiguationData":[TD([[makeQuery(id+"F0.imprint","IMPRINT",EDGE,{"derivedFrom":sQuery(id+"F0.wireOp",EDGE,"E84.bottom")}),1.0]])]});
            var Q108;
            Q108=makeQuery(id+"F0.imprint","IMPRINT",FACE,{"disambiguationData":[TD([[makeQuery(id+"F0.imprint","IMPRINT",EDGE,{"derivedFrom":sQuery(id+"F0.wireOp",EDGE,"E96.bottom")}),1.0]])]});
            var Q109;
            Q109=makeQuery(id+"F0.imprint","IMPRINT",FACE,{"disambiguationData":[TD([[makeQuery(id+"F0.imprint","IMPRINT",EDGE,{"derivedFrom":sQuery(id+"F0.wireOp",EDGE,"E116.bottom")}),-1.0]])]});
            var Q110;
            Q110=makeQuery(id+"F0.imprint","IMPRINT",FACE,{"disambiguationData":[TD([[makeQuery(id+"F0.imprint","IMPRINT",EDGE,{"derivedFrom":sQuery(id+"F0.wireOp",EDGE,"E24.bottom")}),1.0]])]});
            extrude(context, id + "F1", {"entities" : qUnion([Q0, Q1, Q2, Q3, Q4, Q5, Q6, Q7, Q8, Q9, Q10, Q11, Q12, Q13, Q14, Q15, Q16, Q17, Q18, Q19, Q20, Q21, Q22, Q23, Q24, Q25, Q26, Q27, Q28, Q29, Q30, Q31, Q32, Q33, Q34, Q35, Q36, Q37, Q38, Q39, Q40, Q41, Q42, Q43, Q44, Q45, Q46, Q47, Q48, Q49, Q50, Q51, Q52, Q53, Q54, Q55, Q56, Q57, Q58, Q59, Q60, Q61, Q62, Q63, Q64, Q65, Q66, Q67, Q68, Q69, Q70, Q71, Q72, Q73, Q74, Q75, Q76, Q77, Q78, Q79, Q80, Q81, Q82, Q83, Q84, Q85, Q86, Q87, Q88, Q89, Q90, Q91, Q92, Q93, Q94, Q95, Q96, Q97, Q98, Q99, Q100, Q101, Q102, Q103, Q104, Q105, Q106, Q107, Q108, Q109, Q110]), "oppositeDirection" : true, "depth" : 2.7 * mm, "offsetDistance" : 25 * mm});
        }
        {
            var Q0;
            Q0=makeQuery(id+"F0.imprint","IMPRINT",FACE,{"disambiguationData":[TD([[makeQuery(id+"F0.imprint","IMPRINT",EDGE,{"derivedFrom":sQuery(id+"F0.wireOp",EDGE,"E108.bottom")}),-1.0]])]});
            var Q1;
            Q1=makeQuery(id+"F0.imprint","IMPRINT",FACE,{"disambiguationData":[TD([[makeQuery(id+"F0.imprint","IMPRINT",EDGE,{"derivedFrom":sQuery(id+"F0.wireOp",EDGE,"E109.bottom")}),-1.0]])]});
            var Q2;
            Q2=makeQuery(id+"F0.imprint","IMPRINT",FACE,{"disambiguationData":[TD([[makeQuery(id+"F0.imprint","IMPRINT",EDGE,{"derivedFrom":sQuery(id+"F0.wireOp",EDGE,"E110.bottom")}),-1.0]])]});
            var Q3;
            Q3=makeQuery(id+"F0.imprint","IMPRINT",FACE,{"disambiguationData":[TD([[makeQuery(id+"F0.imprint","IMPRINT",EDGE,{"derivedFrom":sQuery(id+"F0.wireOp",EDGE,"E111.bottom")}),-1.0]])]});
            var Q4;
            Q4=makeQuery(id+"F0.imprint","IMPRINT",FACE,{"disambiguationData":[TD([[makeQuery(id+"F0.imprint","IMPRINT",EDGE,{"derivedFrom":sQuery(id+"F0.wireOp",EDGE,"E112.bottom")}),-1.0]])]});
            var Q5;
            Q5=makeQuery(id+"F0.imprint","IMPRINT",FACE,{"disambiguationData":[TD([[makeQuery(id+"F0.imprint","IMPRINT",EDGE,{"derivedFrom":sQuery(id+"F0.wireOp",EDGE,"E113.bottom")}),-1.0]])]});
            var Q6;
            Q6=makeQuery(id+"F0.imprint","IMPRINT",FACE,{"disambiguationData":[TD([[makeQuery(id+"F0.imprint","IMPRINT",EDGE,{"derivedFrom":sQuery(id+"F0.wireOp",EDGE,"E114.bottom")}),-1.0]])]});
            var Q7;
            Q7=makeQuery(id+"F0.imprint","IMPRINT",FACE,{"disambiguationData":[TD([[makeQuery(id+"F0.imprint","IMPRINT",EDGE,{"derivedFrom":sQuery(id+"F0.wireOp",EDGE,"E115.bottom")}),-1.0]])]});
            var Q8;
            Q8=makeQuery(id+"F0.imprint","IMPRINT",FACE,{"disambiguationData":[TD([[makeQuery(id+"F0.imprint","IMPRINT",EDGE,{"derivedFrom":sQuery(id+"F0.wireOp",EDGE,"E116.bottom")}),-1.0]])]});
            var Q9;
            Q9=makeQuery(id+"F0.imprint","IMPRINT",FACE,{"disambiguationData":[TD([[makeQuery(id+"F0.imprint","IMPRINT",EDGE,{"derivedFrom":sQuery(id+"F0.wireOp",EDGE,"E117.bottom")}),-1.0]])]});
            var Q10;
            Q10=makeQuery(id+"F0.imprint","IMPRINT",FACE,{"disambiguationData":[TD([[makeQuery(id+"F0.imprint","IMPRINT",EDGE,{"derivedFrom":sQuery(id+"F0.wireOp",EDGE,"E118.bottom")}),-1.0]])]});
            var Q11;
            Q11=makeQuery(id+"F0.imprint","IMPRINT",FACE,{"disambiguationData":[TD([[makeQuery(id+"F0.imprint","IMPRINT",EDGE,{"derivedFrom":sQuery(id+"F0.wireOp",EDGE,"E119.bottom")}),-1.0]])]});
            var Q12;
            Q12=makeQuery(id+"F0.imprint","IMPRINT",FACE,{"disambiguationData":[TD([[makeQuery(id+"F0.imprint","IMPRINT",EDGE,{"derivedFrom":sQuery(id+"F0.wireOp",EDGE,"E120.bottom")}),-1.0]])]});
            var Q13;
            Q13=makeQuery(id+"F0.imprint","IMPRINT",FACE,{"disambiguationData":[TD([[makeQuery(id+"F0.imprint","IMPRINT",EDGE,{"derivedFrom":sQuery(id+"F0.wireOp",EDGE,"E121.bottom")}),-1.0]])]});
            var Q14;
            Q14=makeQuery(id+"F0.imprint","IMPRINT",FACE,{"disambiguationData":[TD([[makeQuery(id+"F0.imprint","IMPRINT",EDGE,{"derivedFrom":sQuery(id+"F0.wireOp",EDGE,"E21.bottom")}),1.0]])]});
            var Q15;
            Q15=makeQuery(id+"F0.imprint","IMPRINT",FACE,{"disambiguationData":[TD([[makeQuery(id+"F0.imprint","IMPRINT",EDGE,{"derivedFrom":sQuery(id+"F0.wireOp",EDGE,"E20.bottom")}),1.0]])]});
            var Q16;
            Q16=makeQuery(id+"F0.imprint","IMPRINT",FACE,{"disambiguationData":[TD([[makeQuery(id+"F0.imprint","IMPRINT",EDGE,{"derivedFrom":sQuery(id+"F0.wireOp",EDGE,"E19.bottom")}),1.0]])]});
            var Q17;
            Q17=makeQuery(id+"F0.imprint","IMPRINT",FACE,{"disambiguationData":[TD([[makeQuery(id+"F0.imprint","IMPRINT",EDGE,{"derivedFrom":sQuery(id+"F0.wireOp",EDGE,"E16.bottom")}),1.0]])]});
            var Q18;
            Q18=makeQuery(id+"F0.imprint","IMPRINT",FACE,{"disambiguationData":[TD([[makeQuery(id+"F0.imprint","IMPRINT",EDGE,{"derivedFrom":sQuery(id+"F0.wireOp",EDGE,"E17.bottom")}),1.0]])]});
            var Q19;
            Q19=makeQuery(id+"F0.imprint","IMPRINT",FACE,{"disambiguationData":[TD([[makeQuery(id+"F0.imprint","IMPRINT",EDGE,{"derivedFrom":sQuery(id+"F0.wireOp",EDGE,"E18.bottom")}),1.0]])]});
            var Q20;
            Q20=makeQuery(id+"F0.imprint","IMPRINT",FACE,{"disambiguationData":[TD([[makeQuery(id+"F0.imprint","IMPRINT",EDGE,{"derivedFrom":sQuery(id+"F0.wireOp",EDGE,"E15.bottom")}),1.0]])]});
            var Q21;
            Q21=makeQuery(id+"F0.imprint","IMPRINT",FACE,{"disambiguationData":[TD([[makeQuery(id+"F0.imprint","IMPRINT",EDGE,{"derivedFrom":sQuery(id+"F0.wireOp",EDGE,"E29.bottom")}),1.0]])]});
            var Q22;
            Q22=makeQuery(id+"F0.imprint","IMPRINT",FACE,{"disambiguationData":[TD([[makeQuery(id+"F0.imprint","IMPRINT",EDGE,{"derivedFrom":sQuery(id+"F0.wireOp",EDGE,"E124")}),1.0]])]});
            var Q23;
            Q23=makeQuery(id+"F0.imprint","IMPRINT",FACE,{"disambiguationData":[TD([[makeQuery(id+"F0.imprint","IMPRINT",EDGE,{"derivedFrom":sQuery(id+"F0.wireOp",EDGE,"E28.bottom")}),1.0]])]});
            var Q24;
            Q24=makeQuery(id+"F0.imprint","IMPRINT",FACE,{"disambiguationData":[TD([[makeQuery(id+"F0.imprint","IMPRINT",EDGE,{"derivedFrom":sQuery(id+"F0.wireOp",EDGE,"E25.bottom")}),1.0]])]});
            var Q25;
            Q25=makeQuery(id+"F0.imprint","IMPRINT",FACE,{"disambiguationData":[TD([[makeQuery(id+"F0.imprint","IMPRINT",EDGE,{"derivedFrom":sQuery(id+"F0.wireOp",EDGE,"E24.bottom")}),1.0]])]});
            var Q26;
            Q26=makeQuery(id+"F0.imprint","IMPRINT",FACE,{"disambiguationData":[TD([[makeQuery(id+"F0.imprint","IMPRINT",EDGE,{"derivedFrom":sQuery(id+"F0.wireOp",EDGE,"E23.bottom")}),1.0]])]});
            var Q27;
            Q27=makeQuery(id+"F0.imprint","IMPRINT",FACE,{"disambiguationData":[TD([[makeQuery(id+"F0.imprint","IMPRINT",EDGE,{"derivedFrom":sQuery(id+"F0.wireOp",EDGE,"E22.bottom")}),1.0]])]});
            var Q28;
            Q28=makeQuery(id+"F0.imprint","IMPRINT",FACE,{"disambiguationData":[TD([[makeQuery(id+"F0.imprint","IMPRINT",EDGE,{"derivedFrom":sQuery(id+"F0.wireOp",EDGE,"E27.bottom")}),1.0]])]});
            var Q29;
            Q29=makeQuery(id+"F0.imprint","IMPRINT",FACE,{"disambiguationData":[TD([[makeQuery(id+"F0.imprint","IMPRINT",EDGE,{"derivedFrom":sQuery(id+"F0.wireOp",EDGE,"E26.bottom")}),1.0]])]});
            var Q30;
            Q30=makeQuery(id+"F0.imprint","IMPRINT",FACE,{"disambiguationData":[TD([[makeQuery(id+"F0.imprint","IMPRINT",EDGE,{"derivedFrom":sQuery(id+"F0.wireOp",EDGE,"E30.bottom")}),1.0]])]});
            var Q31;
            Q31=makeQuery(id+"F0.imprint","IMPRINT",FACE,{"disambiguationData":[TD([[makeQuery(id+"F0.imprint","IMPRINT",EDGE,{"derivedFrom":sQuery(id+"F0.wireOp",EDGE,"E31.bottom")}),1.0]])]});
            var Q32;
            Q32=makeQuery(id+"F0.imprint","IMPRINT",FACE,{"disambiguationData":[TD([[makeQuery(id+"F0.imprint","IMPRINT",EDGE,{"derivedFrom":sQuery(id+"F0.wireOp",EDGE,"E32.bottom")}),1.0]])]});
            var Q33;
            Q33=makeQuery(id+"F0.imprint","IMPRINT",FACE,{"disambiguationData":[TD([[makeQuery(id+"F0.imprint","IMPRINT",EDGE,{"derivedFrom":sQuery(id+"F0.wireOp",EDGE,"E33.bottom")}),1.0]])]});
            var Q34;
            Q34=makeQuery(id+"F0.imprint","IMPRINT",FACE,{"disambiguationData":[TD([[makeQuery(id+"F0.imprint","IMPRINT",EDGE,{"derivedFrom":sQuery(id+"F0.wireOp",EDGE,"E35.bottom")}),1.0]])]});
            var Q35;
            Q35=makeQuery(id+"F0.imprint","IMPRINT",FACE,{"disambiguationData":[TD([[makeQuery(id+"F0.imprint","IMPRINT",EDGE,{"derivedFrom":sQuery(id+"F0.wireOp",EDGE,"E34.bottom")}),1.0]])]});
            var Q36;
            Q36=makeQuery(id+"F0.imprint","IMPRINT",FACE,{"disambiguationData":[TD([[makeQuery(id+"F0.imprint","IMPRINT",EDGE,{"derivedFrom":sQuery(id+"F0.wireOp",EDGE,"E36.bottom")}),1.0]])]});
            var Q37;
            Q37=makeQuery(id+"F0.imprint","IMPRINT",FACE,{"disambiguationData":[TD([[makeQuery(id+"F0.imprint","IMPRINT",EDGE,{"derivedFrom":sQuery(id+"F0.wireOp",EDGE,"E37.bottom")}),1.0]])]});
            var Q38;
            Q38=makeQuery(id+"F0.imprint","IMPRINT",FACE,{"disambiguationData":[TD([[makeQuery(id+"F0.imprint","IMPRINT",EDGE,{"derivedFrom":sQuery(id+"F0.wireOp",EDGE,"E38.bottom")}),1.0]])]});
            var Q39;
            Q39=makeQuery(id+"F0.imprint","IMPRINT",FACE,{"disambiguationData":[TD([[makeQuery(id+"F0.imprint","IMPRINT",EDGE,{"derivedFrom":sQuery(id+"F0.wireOp",EDGE,"E63.bottom")}),1.0]])]});
            var Q40;
            Q40=makeQuery(id+"F0.imprint","IMPRINT",FACE,{"disambiguationData":[TD([[makeQuery(id+"F0.imprint","IMPRINT",EDGE,{"derivedFrom":sQuery(id+"F0.wireOp",EDGE,"E64.bottom")}),1.0]])]});
            var Q41;
            Q41=makeQuery(id+"F0.imprint","IMPRINT",FACE,{"disambiguationData":[TD([[makeQuery(id+"F0.imprint","IMPRINT",EDGE,{"derivedFrom":sQuery(id+"F0.wireOp",EDGE,"E92.bottom")}),1.0]])]});
            var Q42;
            Q42=makeQuery(id+"F0.imprint","IMPRINT",FACE,{"disambiguationData":[TD([[makeQuery(id+"F0.imprint","IMPRINT",EDGE,{"derivedFrom":sQuery(id+"F0.wireOp",EDGE,"E93.bottom")}),1.0]])]});
            var Q43;
            Q43=makeQuery(id+"F0.imprint","IMPRINT",FACE,{"disambiguationData":[TD([[makeQuery(id+"F0.imprint","IMPRINT",EDGE,{"derivedFrom":sQuery(id+"F0.wireOp",EDGE,"E94.bottom")}),1.0]])]});
            var Q44;
            Q44=makeQuery(id+"F0.imprint","IMPRINT",FACE,{"disambiguationData":[TD([[makeQuery(id+"F0.imprint","IMPRINT",EDGE,{"derivedFrom":sQuery(id+"F0.wireOp",EDGE,"E91.bottom")}),1.0]])]});
            var Q45;
            Q45=makeQuery(id+"F0.imprint","IMPRINT",FACE,{"disambiguationData":[TD([[makeQuery(id+"F0.imprint","IMPRINT",EDGE,{"derivedFrom":sQuery(id+"F0.wireOp",EDGE,"E65.bottom")}),1.0]])]});
            var Q46;
            Q46=makeQuery(id+"F0.imprint","IMPRINT",FACE,{"disambiguationData":[TD([[makeQuery(id+"F0.imprint","IMPRINT",EDGE,{"derivedFrom":sQuery(id+"F0.wireOp",EDGE,"E62.bottom")}),1.0]])]});
            var Q47;
            Q47=makeQuery(id+"F0.imprint","IMPRINT",FACE,{"disambiguationData":[TD([[makeQuery(id+"F0.imprint","IMPRINT",EDGE,{"derivedFrom":sQuery(id+"F0.wireOp",EDGE,"E39.bottom")}),1.0]])]});
            var Q48;
            Q48=makeQuery(id+"F0.imprint","IMPRINT",FACE,{"disambiguationData":[TD([[makeQuery(id+"F0.imprint","IMPRINT",EDGE,{"derivedFrom":sQuery(id+"F0.wireOp",EDGE,"E40.bottom")}),1.0]])]});
            var Q49;
            Q49=makeQuery(id+"F0.imprint","IMPRINT",FACE,{"disambiguationData":[TD([[makeQuery(id+"F0.imprint","IMPRINT",EDGE,{"derivedFrom":sQuery(id+"F0.wireOp",EDGE,"E61.bottom")}),1.0]])]});
            var Q50;
            Q50=makeQuery(id+"F0.imprint","IMPRINT",FACE,{"disambiguationData":[TD([[makeQuery(id+"F0.imprint","IMPRINT",EDGE,{"derivedFrom":sQuery(id+"F0.wireOp",EDGE,"E66.bottom")}),1.0]])]});
            var Q51;
            Q51=makeQuery(id+"F0.imprint","IMPRINT",FACE,{"disambiguationData":[TD([[makeQuery(id+"F0.imprint","IMPRINT",EDGE,{"derivedFrom":sQuery(id+"F0.wireOp",EDGE,"E90.bottom")}),1.0]])]});
            var Q52;
            Q52=makeQuery(id+"F0.imprint","IMPRINT",FACE,{"disambiguationData":[TD([[makeQuery(id+"F0.imprint","IMPRINT",EDGE,{"derivedFrom":sQuery(id+"F0.wireOp",EDGE,"E95.bottom")}),1.0]])]});
            var Q53;
            Q53=makeQuery(id+"F0.imprint","IMPRINT",FACE,{"disambiguationData":[TD([[makeQuery(id+"F0.imprint","IMPRINT",EDGE,{"derivedFrom":sQuery(id+"F0.wireOp",EDGE,"E96.bottom")}),1.0]])]});
            var Q54;
            Q54=makeQuery(id+"F0.imprint","IMPRINT",FACE,{"disambiguationData":[TD([[makeQuery(id+"F0.imprint","IMPRINT",EDGE,{"derivedFrom":sQuery(id+"F0.wireOp",EDGE,"E89.bottom")}),1.0]])]});
            var Q55;
            Q55=makeQuery(id+"F0.imprint","IMPRINT",FACE,{"disambiguationData":[TD([[makeQuery(id+"F0.imprint","IMPRINT",EDGE,{"derivedFrom":sQuery(id+"F0.wireOp",EDGE,"E67.bottom")}),1.0]])]});
            var Q56;
            Q56=makeQuery(id+"F0.imprint","IMPRINT",FACE,{"disambiguationData":[TD([[makeQuery(id+"F0.imprint","IMPRINT",EDGE,{"derivedFrom":sQuery(id+"F0.wireOp",EDGE,"E60.bottom")}),1.0]])]});
            var Q57;
            Q57=makeQuery(id+"F0.imprint","IMPRINT",FACE,{"disambiguationData":[TD([[makeQuery(id+"F0.imprint","IMPRINT",EDGE,{"derivedFrom":sQuery(id+"F0.wireOp",EDGE,"E41.bottom")}),1.0]])]});
            var Q58;
            Q58=makeQuery(id+"F0.imprint","IMPRINT",FACE,{"disambiguationData":[TD([[makeQuery(id+"F0.imprint","IMPRINT",EDGE,{"derivedFrom":sQuery(id+"F0.wireOp",EDGE,"E42.bottom")}),1.0]])]});
            var Q59;
            Q59=makeQuery(id+"F0.imprint","IMPRINT",FACE,{"disambiguationData":[TD([[makeQuery(id+"F0.imprint","IMPRINT",EDGE,{"derivedFrom":sQuery(id+"F0.wireOp",EDGE,"E43.bottom")}),1.0]])]});
            var Q60;
            Q60=makeQuery(id+"F0.imprint","IMPRINT",FACE,{"disambiguationData":[TD([[makeQuery(id+"F0.imprint","IMPRINT",EDGE,{"derivedFrom":sQuery(id+"F0.wireOp",EDGE,"E44.bottom")}),1.0]])]});
            var Q61;
            Q61=makeQuery(id+"F0.imprint","IMPRINT",FACE,{"disambiguationData":[TD([[makeQuery(id+"F0.imprint","IMPRINT",EDGE,{"derivedFrom":sQuery(id+"F0.wireOp",EDGE,"E45.bottom")}),1.0]])]});
            var Q62;
            Q62=makeQuery(id+"F0.imprint","IMPRINT",FACE,{"disambiguationData":[TD([[makeQuery(id+"F0.imprint","IMPRINT",EDGE,{"derivedFrom":sQuery(id+"F0.wireOp",EDGE,"E46.bottom")}),1.0]])]});
            var Q63;
            Q63=makeQuery(id+"F0.imprint","IMPRINT",FACE,{"disambiguationData":[TD([[makeQuery(id+"F0.imprint","IMPRINT",EDGE,{"derivedFrom":sQuery(id+"F0.wireOp",EDGE,"E47.bottom")}),1.0]])]});
            var Q64;
            Q64=makeQuery(id+"F0.imprint","IMPRINT",FACE,{"disambiguationData":[TD([[makeQuery(id+"F0.imprint","IMPRINT",EDGE,{"derivedFrom":sQuery(id+"F0.wireOp",EDGE,"E48.bottom")}),1.0]])]});
            var Q65;
            Q65=makeQuery(id+"F0.imprint","IMPRINT",FACE,{"disambiguationData":[TD([[makeQuery(id+"F0.imprint","IMPRINT",EDGE,{"derivedFrom":sQuery(id+"F0.wireOp",EDGE,"E49.bottom")}),1.0]])]});
            var Q66;
            Q66=makeQuery(id+"F0.imprint","IMPRINT",FACE,{"disambiguationData":[TD([[makeQuery(id+"F0.imprint","IMPRINT",EDGE,{"derivedFrom":sQuery(id+"F0.wireOp",EDGE,"E50.bottom")}),1.0]])]});
            var Q67;
            Q67=makeQuery(id+"F0.imprint","IMPRINT",FACE,{"disambiguationData":[TD([[makeQuery(id+"F0.imprint","IMPRINT",EDGE,{"derivedFrom":sQuery(id+"F0.wireOp",EDGE,"E51.bottom")}),1.0]])]});
            var Q68;
            Q68=makeQuery(id+"F0.imprint","IMPRINT",FACE,{"disambiguationData":[TD([[makeQuery(id+"F0.imprint","IMPRINT",EDGE,{"derivedFrom":sQuery(id+"F0.wireOp",EDGE,"E52.bottom")}),1.0]])]});
            var Q69;
            Q69=makeQuery(id+"F0.imprint","IMPRINT",FACE,{"disambiguationData":[TD([[makeQuery(id+"F0.imprint","IMPRINT",EDGE,{"derivedFrom":sQuery(id+"F0.wireOp",EDGE,"E53.bottom")}),1.0]])]});
            var Q70;
            Q70=makeQuery(id+"F0.imprint","IMPRINT",FACE,{"disambiguationData":[TD([[makeQuery(id+"F0.imprint","IMPRINT",EDGE,{"derivedFrom":sQuery(id+"F0.wireOp",EDGE,"E54.bottom")}),1.0]])]});
            var Q71;
            Q71=makeQuery(id+"F0.imprint","IMPRINT",FACE,{"disambiguationData":[TD([[makeQuery(id+"F0.imprint","IMPRINT",EDGE,{"derivedFrom":sQuery(id+"F0.wireOp",EDGE,"E55.bottom")}),1.0]])]});
            var Q72;
            Q72=makeQuery(id+"F0.imprint","IMPRINT",FACE,{"disambiguationData":[TD([[makeQuery(id+"F0.imprint","IMPRINT",EDGE,{"derivedFrom":sQuery(id+"F0.wireOp",EDGE,"E56.bottom")}),1.0]])]});
            var Q73;
            Q73=makeQuery(id+"F0.imprint","IMPRINT",FACE,{"disambiguationData":[TD([[makeQuery(id+"F0.imprint","IMPRINT",EDGE,{"derivedFrom":sQuery(id+"F0.wireOp",EDGE,"E57.bottom")}),1.0]])]});
            var Q74;
            Q74=makeQuery(id+"F0.imprint","IMPRINT",FACE,{"disambiguationData":[TD([[makeQuery(id+"F0.imprint","IMPRINT",EDGE,{"derivedFrom":sQuery(id+"F0.wireOp",EDGE,"E58.bottom")}),1.0]])]});
            var Q75;
            Q75=makeQuery(id+"F0.imprint","IMPRINT",FACE,{"disambiguationData":[TD([[makeQuery(id+"F0.imprint","IMPRINT",EDGE,{"derivedFrom":sQuery(id+"F0.wireOp",EDGE,"E59.bottom")}),1.0]])]});
            var Q76;
            Q76=makeQuery(id+"F0.imprint","IMPRINT",FACE,{"disambiguationData":[TD([[makeQuery(id+"F0.imprint","IMPRINT",EDGE,{"derivedFrom":sQuery(id+"F0.wireOp",EDGE,"E68.bottom")}),1.0]])]});
            var Q77;
            Q77=makeQuery(id+"F0.imprint","IMPRINT",FACE,{"disambiguationData":[TD([[makeQuery(id+"F0.imprint","IMPRINT",EDGE,{"derivedFrom":sQuery(id+"F0.wireOp",EDGE,"E69.bottom")}),1.0]])]});
            var Q78;
            Q78=makeQuery(id+"F0.imprint","IMPRINT",FACE,{"disambiguationData":[TD([[makeQuery(id+"F0.imprint","IMPRINT",EDGE,{"derivedFrom":sQuery(id+"F0.wireOp",EDGE,"E70.bottom")}),1.0]])]});
            var Q79;
            Q79=makeQuery(id+"F0.imprint","IMPRINT",FACE,{"disambiguationData":[TD([[makeQuery(id+"F0.imprint","IMPRINT",EDGE,{"derivedFrom":sQuery(id+"F0.wireOp",EDGE,"E71.bottom")}),1.0]])]});
            var Q80;
            Q80=makeQuery(id+"F0.imprint","IMPRINT",FACE,{"disambiguationData":[TD([[makeQuery(id+"F0.imprint","IMPRINT",EDGE,{"derivedFrom":sQuery(id+"F0.wireOp",EDGE,"E72.bottom")}),1.0]])]});
            var Q81;
            Q81=makeQuery(id+"F0.imprint","IMPRINT",FACE,{"disambiguationData":[TD([[makeQuery(id+"F0.imprint","IMPRINT",EDGE,{"derivedFrom":sQuery(id+"F0.wireOp",EDGE,"E73.bottom")}),1.0]])]});
            var Q82;
            Q82=makeQuery(id+"F0.imprint","IMPRINT",FACE,{"disambiguationData":[TD([[makeQuery(id+"F0.imprint","IMPRINT",EDGE,{"derivedFrom":sQuery(id+"F0.wireOp",EDGE,"E74.bottom")}),1.0]])]});
            var Q83;
            Q83=makeQuery(id+"F0.imprint","IMPRINT",FACE,{"disambiguationData":[TD([[makeQuery(id+"F0.imprint","IMPRINT",EDGE,{"derivedFrom":sQuery(id+"F0.wireOp",EDGE,"E75.bottom")}),1.0]])]});
            var Q84;
            Q84=makeQuery(id+"F0.imprint","IMPRINT",FACE,{"disambiguationData":[TD([[makeQuery(id+"F0.imprint","IMPRINT",EDGE,{"derivedFrom":sQuery(id+"F0.wireOp",EDGE,"E76.bottom")}),1.0]])]});
            var Q85;
            Q85=makeQuery(id+"F0.imprint","IMPRINT",FACE,{"disambiguationData":[TD([[makeQuery(id+"F0.imprint","IMPRINT",EDGE,{"derivedFrom":sQuery(id+"F0.wireOp",EDGE,"E77.bottom")}),1.0]])]});
            var Q86;
            Q86=makeQuery(id+"F0.imprint","IMPRINT",FACE,{"disambiguationData":[TD([[makeQuery(id+"F0.imprint","IMPRINT",EDGE,{"derivedFrom":sQuery(id+"F0.wireOp",EDGE,"E78.bottom")}),1.0]])]});
            var Q87;
            Q87=makeQuery(id+"F0.imprint","IMPRINT",FACE,{"disambiguationData":[TD([[makeQuery(id+"F0.imprint","IMPRINT",EDGE,{"derivedFrom":sQuery(id+"F0.wireOp",EDGE,"E79.bottom")}),1.0]])]});
            var Q88;
            Q88=makeQuery(id+"F0.imprint","IMPRINT",FACE,{"disambiguationData":[TD([[makeQuery(id+"F0.imprint","IMPRINT",EDGE,{"derivedFrom":sQuery(id+"F0.wireOp",EDGE,"E80.bottom")}),1.0]])]});
            var Q89;
            Q89=makeQuery(id+"F0.imprint","IMPRINT",FACE,{"disambiguationData":[TD([[makeQuery(id+"F0.imprint","IMPRINT",EDGE,{"derivedFrom":sQuery(id+"F0.wireOp",EDGE,"E81.bottom")}),1.0]])]});
            var Q90;
            Q90=makeQuery(id+"F0.imprint","IMPRINT",FACE,{"disambiguationData":[TD([[makeQuery(id+"F0.imprint","IMPRINT",EDGE,{"derivedFrom":sQuery(id+"F0.wireOp",EDGE,"E82.bottom")}),1.0]])]});
            var Q91;
            Q91=makeQuery(id+"F0.imprint","IMPRINT",FACE,{"disambiguationData":[TD([[makeQuery(id+"F0.imprint","IMPRINT",EDGE,{"derivedFrom":sQuery(id+"F0.wireOp",EDGE,"E83.bottom")}),1.0]])]});
            var Q92;
            Q92=makeQuery(id+"F0.imprint","IMPRINT",FACE,{"disambiguationData":[TD([[makeQuery(id+"F0.imprint","IMPRINT",EDGE,{"derivedFrom":sQuery(id+"F0.wireOp",EDGE,"E84.bottom")}),1.0]])]});
            var Q93;
            Q93=makeQuery(id+"F0.imprint","IMPRINT",FACE,{"disambiguationData":[TD([[makeQuery(id+"F0.imprint","IMPRINT",EDGE,{"derivedFrom":sQuery(id+"F0.wireOp",EDGE,"E85.bottom")}),1.0]])]});
            var Q94;
            Q94=makeQuery(id+"F0.imprint","IMPRINT",FACE,{"disambiguationData":[TD([[makeQuery(id+"F0.imprint","IMPRINT",EDGE,{"derivedFrom":sQuery(id+"F0.wireOp",EDGE,"E86.bottom")}),1.0]])]});
            var Q95;
            Q95=makeQuery(id+"F0.imprint","IMPRINT",FACE,{"disambiguationData":[TD([[makeQuery(id+"F0.imprint","IMPRINT",EDGE,{"derivedFrom":sQuery(id+"F0.wireOp",EDGE,"E87.bottom")}),1.0]])]});
            var Q96;
            Q96=makeQuery(id+"F0.imprint","IMPRINT",FACE,{"disambiguationData":[TD([[makeQuery(id+"F0.imprint","IMPRINT",EDGE,{"derivedFrom":sQuery(id+"F0.wireOp",EDGE,"E88.bottom")}),1.0]])]});
            var Q97;
            Q97=makeQuery(id+"F0.imprint","IMPRINT",FACE,{"disambiguationData":[TD([[makeQuery(id+"F0.imprint","IMPRINT",EDGE,{"derivedFrom":sQuery(id+"F0.wireOp",EDGE,"E97.bottom")}),1.0]])]});
            var Q98;
            Q98=makeQuery(id+"F0.imprint","IMPRINT",FACE,{"disambiguationData":[TD([[makeQuery(id+"F0.imprint","IMPRINT",EDGE,{"derivedFrom":sQuery(id+"F0.wireOp",EDGE,"E98.bottom")}),1.0]])]});
            var Q99;
            Q99=makeQuery(id+"F0.imprint","IMPRINT",FACE,{"disambiguationData":[TD([[makeQuery(id+"F0.imprint","IMPRINT",EDGE,{"derivedFrom":sQuery(id+"F0.wireOp",EDGE,"E99.bottom")}),1.0]])]});
            var Q100;
            Q100=makeQuery(id+"F0.imprint","IMPRINT",FACE,{"disambiguationData":[TD([[makeQuery(id+"F0.imprint","IMPRINT",EDGE,{"derivedFrom":sQuery(id+"F0.wireOp",EDGE,"E100.bottom")}),1.0]])]});
            var Q101;
            Q101=makeQuery(id+"F0.imprint","IMPRINT",FACE,{"disambiguationData":[TD([[makeQuery(id+"F0.imprint","IMPRINT",EDGE,{"derivedFrom":sQuery(id+"F0.wireOp",EDGE,"E101.bottom")}),1.0]])]});
            var Q102;
            Q102=makeQuery(id+"F0.imprint","IMPRINT",FACE,{"disambiguationData":[TD([[makeQuery(id+"F0.imprint","IMPRINT",EDGE,{"derivedFrom":sQuery(id+"F0.wireOp",EDGE,"E102.bottom")}),1.0]])]});
            var Q103;
            Q103=makeQuery(id+"F0.imprint","IMPRINT",FACE,{"disambiguationData":[TD([[makeQuery(id+"F0.imprint","IMPRINT",EDGE,{"derivedFrom":sQuery(id+"F0.wireOp",EDGE,"E103.bottom")}),1.0]])]});
            var Q104;
            Q104=makeQuery(id+"F0.imprint","IMPRINT",FACE,{"disambiguationData":[TD([[makeQuery(id+"F0.imprint","IMPRINT",EDGE,{"derivedFrom":sQuery(id+"F0.wireOp",EDGE,"E104.bottom")}),1.0]])]});
            var Q105;
            Q105=makeQuery(id+"F0.imprint","IMPRINT",FACE,{"disambiguationData":[TD([[makeQuery(id+"F0.imprint","IMPRINT",EDGE,{"derivedFrom":sQuery(id+"F0.wireOp",EDGE,"E105.bottom")}),1.0]])]});
            var Q106;
            Q106=makeQuery(id+"F0.imprint","IMPRINT",FACE,{"disambiguationData":[TD([[makeQuery(id+"F0.imprint","IMPRINT",EDGE,{"derivedFrom":sQuery(id+"F0.wireOp",EDGE,"E106.bottom")}),1.0]])]});
            var Q107;
            Q107=makeQuery(id+"F0.imprint","IMPRINT",FACE,{"disambiguationData":[TD([[makeQuery(id+"F0.imprint","IMPRINT",EDGE,{"derivedFrom":sQuery(id+"F0.wireOp",EDGE,"E107.bottom")}),1.0]])]});
            extrude(context, id + "F2", {"entities" : qUnion([Q0, Q1, Q2, Q3, Q4, Q5, Q6, Q7, Q8, Q9, Q10, Q11, Q12, Q13, Q14, Q15, Q16, Q17, Q18, Q19, Q20, Q21, Q22, Q23, Q24, Q25, Q26, Q27, Q28, Q29, Q30, Q31, Q32, Q33, Q34, Q35, Q36, Q37, Q38, Q39, Q40, Q41, Q42, Q43, Q44, Q45, Q46, Q47, Q48, Q49, Q50, Q51, Q52, Q53, Q54, Q55, Q56, Q57, Q58, Q59, Q60, Q61, Q62, Q63, Q64, Q65, Q66, Q67, Q68, Q69, Q70, Q71, Q72, Q73, Q74, Q75, Q76, Q77, Q78, Q79, Q80, Q81, Q82, Q83, Q84, Q85, Q86, Q87, Q88, Q89, Q90, Q91, Q92, Q93, Q94, Q95, Q96, Q97, Q98, Q99, Q100, Q101, Q102, Q103, Q104, Q105, Q106, Q107]), "depth" : 3 * mm, "offsetDistance" : 25 * mm});
        }
        {
            var Q0;
            Q0=makeQuery(id+"F0.imprint","IMPRINT",FACE,{"disambiguationData":[TD([[makeQuery(id+"F0.imprint","IMPRINT",EDGE,{"derivedFrom":sQuery(id+"F0.wireOp",EDGE,"E122")}),1.0]])]});
            var Q1;
            Q1=makeQuery(id+"F0.imprint","IMPRINT",FACE,{"disambiguationData":[TD([[makeQuery(id+"F0.imprint","IMPRINT",EDGE,{"derivedFrom":sQuery(id+"F0.wireOp",EDGE,"E123")}),1.0]])]});
            extrude(context, id + "F3", {"entities" : qUnion([Q0, Q1]), "depth" : 3 * mm, "offsetDistance" : 25 * mm});
        }
        {
            var Q0;
            Q0=makeQuery(id+"F1.opExtrude","CAP_FACE",FACE,{"disambiguationData":[OSD([sQuery(id+"F0.wireOp",EDGE,"E0.bottom"),sQuery(id+"F0.wireOp",EDGE,"E0.top"),sQuery(id+"F0.wireOp",EDGE,"E0.left"),sQuery(id+"F0.wireOp",EDGE,"E0.right")])],"isStart":false});
            var sketch = newSketch(context, id + "F4", { "sketchPlane" : qUnion([Q0])});
            skLineSegment(sketch, "E128.bottom", {"start": v(-206, -66) * mm, "end": v(204, -66) * mm});
            skLineSegment(sketch, "E128.top", {"start": v(-206, 66) * mm, "end": v(204, 66) * mm});
            skLineSegment(sketch, "E128.left", {"start": v(-206, -66) * mm, "end": v(-206, 66) * mm});
            skLineSegment(sketch, "E128.right", {"start": v(204, -66) * mm, "end": v(204, 66) * mm});
            skPoint(sketch, "E128.middle", {"position": v(-1, 0) * mm});
            skCircle(sketch, "E129", {"center": v(211, 0) * mm, "radius": 1.5 * mm});
            skCircle(sketch, "E130", {"center": v(211, -71) * mm, "radius": 1.5 * mm});
            skCircle(sketch, "E131", {"center": v(209.94, 71) * mm, "radius": 1.5 * mm});
            skLineSegment(sketch, "E132", {"start": v(216, 0) * mm, "end": v(-216, 0) * mm, "construction": true});
            skCircle(sketch, "E133.1.0.0", {"center": v(126.6, -71) * mm, "radius": 1.5 * mm});
            skCircle(sketch, "E133.1.0.1", {"center": v(125.54, 71) * mm, "radius": 1.5 * mm});
            skCircle(sketch, "E133.2.0.0", {"center": v(42.2, -71) * mm, "radius": 1.5 * mm});
            skCircle(sketch, "E133.2.0.1", {"center": v(41.14, 71) * mm, "radius": 1.5 * mm});
            skCircle(sketch, "E133.3.0.0", {"center": v(-42.2, -71) * mm, "radius": 1.5 * mm});
            skCircle(sketch, "E133.3.0.1", {"center": v(-43.26, 71) * mm, "radius": 1.5 * mm});
            skCircle(sketch, "E133.4.0.0", {"center": v(-126.6, -71) * mm, "radius": 1.5 * mm});
            skCircle(sketch, "E133.4.0.1", {"center": v(-127.66, 71) * mm, "radius": 1.5 * mm});
            skCircle(sketch, "E133.5.0.0", {"center": v(-211, -71) * mm, "radius": 1.5 * mm});
            skCircle(sketch, "E133.5.0.1", {"center": v(-212.06, 71) * mm, "radius": 1.5 * mm});
            skLineSegment(sketch, "E133.direction1", {"start": v(211, -71) * mm, "end": v(126.6, -71) * mm, "construction": true});
            skSolve(sketch);
        }
        {
            var Q0;
            Q0 = qSketchRegion(id + "F4", true);
            extrude(context, id + "F5", {"entities" : qUnion([Q0]), "depth" : 26 * mm, "offsetDistance" : 25 * mm});
        }
    });
